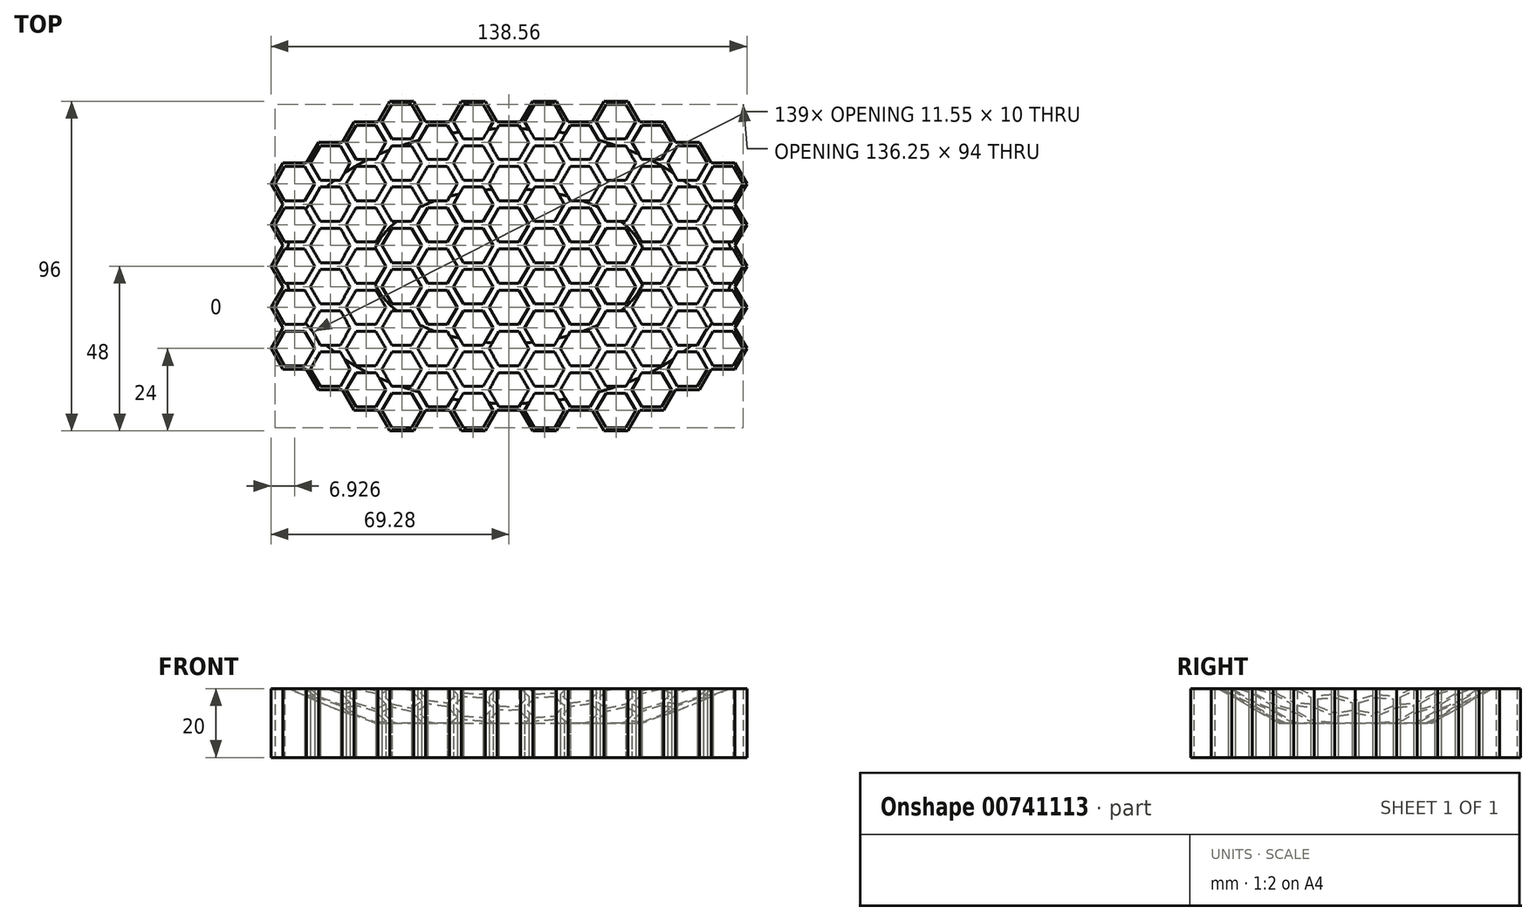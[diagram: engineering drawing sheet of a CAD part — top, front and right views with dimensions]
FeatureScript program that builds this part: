
annotation { "Feature Type Name" : "Feature", "Feature Type Description" : "" }
export const myFeature = defineFeature(function(context is Context, id is Id, definition is map)
    precondition{}
    {
        {
            var Q0;
            Q0=qCreatedBy(makeId("Top.planeOp"),FACE);
            var sketch = newSketch(context, id + "F0", { "sketchPlane" : qUnion([Q0])});
            skLineSegment(sketch, "E0", {"start": v(-3.46, -6) * mm, "end": v(-6.93, 0) * mm, "construction": true});
            skLineSegment(sketch, "E1", {"start": v(-6.93, 0) * mm, "end": v(-3.46, 6) * mm, "construction": true});
            skLineSegment(sketch, "E2", {"start": v(-2.89, 5) * mm, "end": v(2.89, 5) * mm});
            skLineSegment(sketch, "E3", {"start": v(2.89, 5) * mm, "end": v(5.77, 0) * mm});
            skLineSegment(sketch, "E4", {"start": v(5.77, 0) * mm, "end": v(2.89, -5) * mm});
            skLineSegment(sketch, "E5", {"start": v(2.89, -5) * mm, "end": v(-2.89, -5) * mm});
            skLineSegment(sketch, "E6", {"start": v(-2.89, -5) * mm, "end": v(-5.77, 0) * mm});
            skLineSegment(sketch, "E7", {"start": v(-5.77, 0) * mm, "end": v(-2.89, 5) * mm});
            skLineSegment(sketch, "E8", {"start": v(3.46, 6) * mm, "end": v(-3.46, 6) * mm, "construction": true});
            skLineSegment(sketch, "E9", {"start": v(-3.46, -6) * mm, "end": v(3.46, -6) * mm, "construction": true});
            skLineSegment(sketch, "E10", {"start": v(-3.46, 6) * mm, "end": v(-6.93, 12) * mm, "construction": true});
            skLineSegment(sketch, "E11", {"start": v(-6.93, 12) * mm, "end": v(-3.46, 18) * mm, "construction": true});
            skLineSegment(sketch, "E12", {"start": v(-2.89, 17) * mm, "end": v(2.89, 17) * mm});
            skLineSegment(sketch, "E13", {"start": v(2.89, 17) * mm, "end": v(5.77, 12) * mm});
            skLineSegment(sketch, "E14", {"start": v(5.77, 12) * mm, "end": v(2.89, 7) * mm});
            skLineSegment(sketch, "E15", {"start": v(2.89, 7) * mm, "end": v(-2.89, 7) * mm});
            skLineSegment(sketch, "E16", {"start": v(-2.89, 7) * mm, "end": v(-5.77, 12) * mm});
            skLineSegment(sketch, "E17", {"start": v(-5.77, 12) * mm, "end": v(-2.89, 17) * mm});
            skLineSegment(sketch, "E18", {"start": v(3.46, 18) * mm, "end": v(-3.46, 18) * mm, "construction": true});
            skLineSegment(sketch, "E19", {"start": v(3.46, 6) * mm, "end": v(6.93, 12) * mm, "construction": true});
            skLineSegment(sketch, "E20", {"start": v(3.46, 30) * mm, "end": v(6.93, 24) * mm, "construction": true});
            skLineSegment(sketch, "E21", {"start": v(-3.46, 18) * mm, "end": v(-6.93, 24) * mm, "construction": true});
            skLineSegment(sketch, "E22", {"start": v(-6.93, 24) * mm, "end": v(-3.46, 30) * mm, "construction": true});
            skLineSegment(sketch, "E23", {"start": v(-2.89, 29) * mm, "end": v(2.89, 29) * mm});
            skLineSegment(sketch, "E24", {"start": v(2.89, 29) * mm, "end": v(5.77, 24) * mm});
            skLineSegment(sketch, "E25", {"start": v(5.77, 24) * mm, "end": v(2.89, 19) * mm});
            skLineSegment(sketch, "E26", {"start": v(2.89, 19) * mm, "end": v(-2.89, 19) * mm});
            skLineSegment(sketch, "E27", {"start": v(-2.89, 19) * mm, "end": v(-5.77, 24) * mm});
            skLineSegment(sketch, "E28", {"start": v(-5.77, 24) * mm, "end": v(-2.89, 29) * mm});
            skLineSegment(sketch, "E29", {"start": v(3.46, 30) * mm, "end": v(-3.46, 30) * mm, "construction": true});
            skLineSegment(sketch, "E30", {"start": v(-3.46, 30) * mm, "end": v(-6.93, 36) * mm, "construction": true});
            skLineSegment(sketch, "E31", {"start": v(-6.93, 36) * mm, "end": v(-3.46, 42) * mm, "construction": true});
            skLineSegment(sketch, "E32", {"start": v(-2.89, 41) * mm, "end": v(2.89, 41) * mm});
            skLineSegment(sketch, "E33", {"start": v(2.89, 41) * mm, "end": v(5.77, 36) * mm});
            skLineSegment(sketch, "E34", {"start": v(5.77, 36) * mm, "end": v(2.89, 31) * mm});
            skLineSegment(sketch, "E35", {"start": v(2.89, 31) * mm, "end": v(-2.89, 31) * mm});
            skLineSegment(sketch, "E36", {"start": v(-2.89, 31) * mm, "end": v(-5.77, 36) * mm});
            skLineSegment(sketch, "E37", {"start": v(-5.77, 36) * mm, "end": v(-2.89, 41) * mm});
            skLineSegment(sketch, "E38", {"start": v(3.46, 42) * mm, "end": v(-3.46, 42) * mm});
            skLineSegment(sketch, "E39", {"start": v(3.46, 30) * mm, "end": v(6.93, 36) * mm, "construction": true});
            skLineSegment(sketch, "E40", {"start": v(-6.93, -48) * mm, "end": v(-3.46, -42) * mm});
            skLineSegment(sketch, "E41", {"start": v(3.46, -42) * mm, "end": v(-3.46, -42) * mm});
            skLineSegment(sketch, "E42", {"start": v(-3.46, -42) * mm, "end": v(-6.93, -36) * mm, "construction": true});
            skLineSegment(sketch, "E43", {"start": v(-6.93, -36) * mm, "end": v(-3.46, -30) * mm, "construction": true});
            skLineSegment(sketch, "E44", {"start": v(-2.89, -31) * mm, "end": v(2.89, -31) * mm});
            skLineSegment(sketch, "E45", {"start": v(2.89, -31) * mm, "end": v(5.77, -36) * mm});
            skLineSegment(sketch, "E46", {"start": v(5.77, -36) * mm, "end": v(2.89, -41) * mm});
            skLineSegment(sketch, "E47", {"start": v(2.89, -41) * mm, "end": v(-2.89, -41) * mm});
            skLineSegment(sketch, "E48", {"start": v(-2.89, -41) * mm, "end": v(-5.77, -36) * mm});
            skLineSegment(sketch, "E49", {"start": v(-5.77, -36) * mm, "end": v(-2.89, -31) * mm});
            skLineSegment(sketch, "E50", {"start": v(3.46, -30) * mm, "end": v(-3.46, -30) * mm, "construction": true});
            skLineSegment(sketch, "E51", {"start": v(3.46, -42) * mm, "end": v(6.93, -36) * mm, "construction": true});
            skLineSegment(sketch, "E52", {"start": v(3.46, -18) * mm, "end": v(6.93, -24) * mm, "construction": true});
            skLineSegment(sketch, "E53", {"start": v(-3.46, -30) * mm, "end": v(-6.93, -24) * mm, "construction": true});
            skLineSegment(sketch, "E54", {"start": v(-6.93, -24) * mm, "end": v(-3.46, -18) * mm, "construction": true});
            skLineSegment(sketch, "E55", {"start": v(-2.89, -19) * mm, "end": v(2.89, -19) * mm});
            skLineSegment(sketch, "E56", {"start": v(2.89, -19) * mm, "end": v(5.77, -24) * mm});
            skLineSegment(sketch, "E57", {"start": v(5.77, -24) * mm, "end": v(2.89, -29) * mm});
            skLineSegment(sketch, "E58", {"start": v(2.89, -29) * mm, "end": v(-2.89, -29) * mm});
            skLineSegment(sketch, "E59", {"start": v(-2.89, -29) * mm, "end": v(-5.77, -24) * mm});
            skLineSegment(sketch, "E60", {"start": v(-5.77, -24) * mm, "end": v(-2.89, -19) * mm});
            skLineSegment(sketch, "E61", {"start": v(3.46, -18) * mm, "end": v(-3.46, -18) * mm, "construction": true});
            skLineSegment(sketch, "E62", {"start": v(-3.46, -18) * mm, "end": v(-6.93, -12) * mm, "construction": true});
            skLineSegment(sketch, "E63", {"start": v(-6.93, -12) * mm, "end": v(-3.46, -6) * mm, "construction": true});
            skLineSegment(sketch, "E64", {"start": v(-2.89, -7) * mm, "end": v(2.89, -7) * mm});
            skLineSegment(sketch, "E65", {"start": v(2.89, -7) * mm, "end": v(5.77, -12) * mm});
            skLineSegment(sketch, "E66", {"start": v(5.77, -12) * mm, "end": v(2.89, -17) * mm});
            skLineSegment(sketch, "E67", {"start": v(2.89, -17) * mm, "end": v(-2.89, -17) * mm});
            skLineSegment(sketch, "E68", {"start": v(-2.89, -17) * mm, "end": v(-5.77, -12) * mm});
            skLineSegment(sketch, "E69", {"start": v(-5.77, -12) * mm, "end": v(-2.89, -7) * mm});
            skLineSegment(sketch, "E70", {"start": v(3.46, -18) * mm, "end": v(6.93, -12) * mm, "construction": true});
            skLineSegment(sketch, "E71", {"start": v(6.93, 0) * mm, "end": v(3.46, 6) * mm, "construction": true});
            skLineSegment(sketch, "E72", {"start": v(7.5, 11) * mm, "end": v(13.28, 11) * mm});
            skLineSegment(sketch, "E73", {"start": v(13.28, 11) * mm, "end": v(16.17, 6) * mm});
            skLineSegment(sketch, "E74", {"start": v(16.17, 6) * mm, "end": v(13.28, 1) * mm});
            skLineSegment(sketch, "E75", {"start": v(13.28, 1) * mm, "end": v(7.5, 1) * mm});
            skLineSegment(sketch, "E76", {"start": v(7.5, 1) * mm, "end": v(4.62, 6) * mm});
            skLineSegment(sketch, "E77", {"start": v(4.62, 6) * mm, "end": v(7.5, 11) * mm});
            skLineSegment(sketch, "E78", {"start": v(13.86, 12) * mm, "end": v(6.93, 12) * mm, "construction": true});
            skLineSegment(sketch, "E79", {"start": v(6.93, 0) * mm, "end": v(13.86, 0) * mm, "construction": true});
            skLineSegment(sketch, "E80", {"start": v(6.93, 12) * mm, "end": v(3.46, 18) * mm, "construction": true});
            skLineSegment(sketch, "E81", {"start": v(3.46, 18) * mm, "end": v(6.93, 24) * mm, "construction": true});
            skLineSegment(sketch, "E82", {"start": v(7.5, 23) * mm, "end": v(13.28, 23) * mm});
            skLineSegment(sketch, "E83", {"start": v(13.28, 23) * mm, "end": v(16.17, 18) * mm});
            skLineSegment(sketch, "E84", {"start": v(16.17, 18) * mm, "end": v(13.28, 13) * mm});
            skLineSegment(sketch, "E85", {"start": v(13.28, 13) * mm, "end": v(7.5, 13) * mm});
            skLineSegment(sketch, "E86", {"start": v(7.5, 13) * mm, "end": v(4.62, 18) * mm});
            skLineSegment(sketch, "E87", {"start": v(4.62, 18) * mm, "end": v(7.5, 23) * mm});
            skLineSegment(sketch, "E88", {"start": v(13.86, 24) * mm, "end": v(6.93, 24) * mm, "construction": true});
            skLineSegment(sketch, "E89", {"start": v(7.5, 35) * mm, "end": v(13.28, 35) * mm});
            skLineSegment(sketch, "E90", {"start": v(13.28, 35) * mm, "end": v(16.17, 30) * mm});
            skLineSegment(sketch, "E91", {"start": v(16.17, 30) * mm, "end": v(13.28, 25) * mm});
            skLineSegment(sketch, "E92", {"start": v(13.28, 25) * mm, "end": v(7.5, 25) * mm});
            skLineSegment(sketch, "E93", {"start": v(7.5, 25) * mm, "end": v(4.62, 30) * mm});
            skLineSegment(sketch, "E94", {"start": v(4.62, 30) * mm, "end": v(7.5, 35) * mm});
            skLineSegment(sketch, "E95", {"start": v(13.86, 36) * mm, "end": v(6.93, 36) * mm, "construction": true});
            skLineSegment(sketch, "E96", {"start": v(13.86, 24) * mm, "end": v(17.32, 30) * mm, "construction": true});
            skLineSegment(sketch, "E97", {"start": v(13.86, 48) * mm, "end": v(17.32, 42) * mm});
            skLineSegment(sketch, "E98", {"start": v(6.93, 36) * mm, "end": v(3.46, 42) * mm, "construction": true});
            skLineSegment(sketch, "E99", {"start": v(3.46, 42) * mm, "end": v(6.93, 48) * mm});
            skLineSegment(sketch, "E100", {"start": v(7.5, 47) * mm, "end": v(13.28, 47) * mm});
            skLineSegment(sketch, "E101", {"start": v(13.28, 47) * mm, "end": v(16.17, 42) * mm});
            skLineSegment(sketch, "E102", {"start": v(16.17, 42) * mm, "end": v(13.28, 37) * mm});
            skLineSegment(sketch, "E103", {"start": v(13.28, 37) * mm, "end": v(7.5, 37) * mm});
            skLineSegment(sketch, "E104", {"start": v(7.5, 37) * mm, "end": v(4.62, 42) * mm});
            skLineSegment(sketch, "E105", {"start": v(4.62, 42) * mm, "end": v(7.5, 47) * mm});
            skLineSegment(sketch, "E106", {"start": v(13.86, 48) * mm, "end": v(6.93, 48) * mm});
            skLineSegment(sketch, "E107", {"start": v(6.93, -48) * mm, "end": v(3.46, -42) * mm});
            skLineSegment(sketch, "E108", {"start": v(7.5, -37) * mm, "end": v(13.28, -37) * mm});
            skLineSegment(sketch, "E109", {"start": v(13.28, -37) * mm, "end": v(16.17, -42) * mm});
            skLineSegment(sketch, "E110", {"start": v(16.17, -42) * mm, "end": v(13.28, -47) * mm});
            skLineSegment(sketch, "E111", {"start": v(13.28, -47) * mm, "end": v(7.5, -47) * mm});
            skLineSegment(sketch, "E112", {"start": v(7.5, -47) * mm, "end": v(4.62, -42) * mm});
            skLineSegment(sketch, "E113", {"start": v(4.62, -42) * mm, "end": v(7.5, -37) * mm});
            skLineSegment(sketch, "E114", {"start": v(13.86, -36) * mm, "end": v(6.93, -36) * mm, "construction": true});
            skLineSegment(sketch, "E115", {"start": v(6.93, -48) * mm, "end": v(13.86, -48) * mm});
            skLineSegment(sketch, "E116", {"start": v(13.86, -48) * mm, "end": v(17.32, -42) * mm});
            skLineSegment(sketch, "E117", {"start": v(6.93, -36) * mm, "end": v(3.46, -30) * mm, "construction": true});
            skLineSegment(sketch, "E118", {"start": v(3.46, -30) * mm, "end": v(6.93, -24) * mm, "construction": true});
            skLineSegment(sketch, "E119", {"start": v(7.5, -25) * mm, "end": v(13.28, -25) * mm});
            skLineSegment(sketch, "E120", {"start": v(13.28, -25) * mm, "end": v(16.17, -30) * mm});
            skLineSegment(sketch, "E121", {"start": v(16.17, -30) * mm, "end": v(13.28, -35) * mm});
            skLineSegment(sketch, "E122", {"start": v(13.28, -35) * mm, "end": v(7.5, -35) * mm});
            skLineSegment(sketch, "E123", {"start": v(7.5, -35) * mm, "end": v(4.62, -30) * mm});
            skLineSegment(sketch, "E124", {"start": v(4.62, -30) * mm, "end": v(7.5, -25) * mm});
            skLineSegment(sketch, "E125", {"start": v(13.86, -24) * mm, "end": v(6.93, -24) * mm, "construction": true});
            skLineSegment(sketch, "E126", {"start": v(13.86, -36) * mm, "end": v(17.32, -30) * mm, "construction": true});
            skLineSegment(sketch, "E127", {"start": v(13.86, -12) * mm, "end": v(17.32, -18) * mm, "construction": true});
            skLineSegment(sketch, "E128", {"start": v(7.5, -13) * mm, "end": v(13.28, -13) * mm});
            skLineSegment(sketch, "E129", {"start": v(13.28, -13) * mm, "end": v(16.17, -18) * mm});
            skLineSegment(sketch, "E130", {"start": v(16.17, -18) * mm, "end": v(13.28, -23) * mm});
            skLineSegment(sketch, "E131", {"start": v(13.28, -23) * mm, "end": v(7.5, -23) * mm});
            skLineSegment(sketch, "E132", {"start": v(7.5, -23) * mm, "end": v(4.62, -18) * mm});
            skLineSegment(sketch, "E133", {"start": v(4.62, -18) * mm, "end": v(7.5, -13) * mm});
            skLineSegment(sketch, "E134", {"start": v(13.86, -12) * mm, "end": v(6.93, -12) * mm, "construction": true});
            skLineSegment(sketch, "E135", {"start": v(6.93, -12) * mm, "end": v(3.46, -6) * mm, "construction": true});
            skLineSegment(sketch, "E136", {"start": v(3.46, -6) * mm, "end": v(6.93, 0) * mm, "construction": true});
            skLineSegment(sketch, "E137", {"start": v(7.5, -1) * mm, "end": v(13.28, -1) * mm});
            skLineSegment(sketch, "E138", {"start": v(13.28, -1) * mm, "end": v(16.17, -6) * mm});
            skLineSegment(sketch, "E139", {"start": v(16.17, -6) * mm, "end": v(13.28, -11) * mm});
            skLineSegment(sketch, "E140", {"start": v(13.28, -11) * mm, "end": v(7.5, -11) * mm});
            skLineSegment(sketch, "E141", {"start": v(7.5, -11) * mm, "end": v(4.62, -6) * mm});
            skLineSegment(sketch, "E142", {"start": v(4.62, -6) * mm, "end": v(7.5, -1) * mm});
            skLineSegment(sketch, "E143", {"start": v(13.86, -12) * mm, "end": v(17.32, -6) * mm, "construction": true});
            skLineSegment(sketch, "E144", {"start": v(17.32, -6) * mm, "end": v(13.86, 0) * mm, "construction": true});
            skLineSegment(sketch, "E145", {"start": v(13.86, 0) * mm, "end": v(17.32, 6) * mm, "construction": true});
            skLineSegment(sketch, "E146", {"start": v(17.9, 5) * mm, "end": v(23.67, 5) * mm});
            skLineSegment(sketch, "E147", {"start": v(23.67, 5) * mm, "end": v(26.56, 0) * mm});
            skLineSegment(sketch, "E148", {"start": v(26.56, 0) * mm, "end": v(23.67, -5) * mm});
            skLineSegment(sketch, "E149", {"start": v(23.67, -5) * mm, "end": v(17.9, -5) * mm});
            skLineSegment(sketch, "E150", {"start": v(17.9, -5) * mm, "end": v(15.01, 0) * mm});
            skLineSegment(sketch, "E151", {"start": v(15.01, 0) * mm, "end": v(17.9, 5) * mm});
            skLineSegment(sketch, "E152", {"start": v(24.25, 6) * mm, "end": v(17.32, 6) * mm, "construction": true});
            skLineSegment(sketch, "E153", {"start": v(17.32, -6) * mm, "end": v(24.25, -6) * mm, "construction": true});
            skLineSegment(sketch, "E154", {"start": v(17.32, 6) * mm, "end": v(13.86, 12) * mm, "construction": true});
            skLineSegment(sketch, "E155", {"start": v(13.86, 12) * mm, "end": v(17.32, 18) * mm, "construction": true});
            skLineSegment(sketch, "E156", {"start": v(17.9, 17) * mm, "end": v(23.67, 17) * mm});
            skLineSegment(sketch, "E157", {"start": v(23.67, 17) * mm, "end": v(26.56, 12) * mm});
            skLineSegment(sketch, "E158", {"start": v(26.56, 12) * mm, "end": v(23.67, 7) * mm});
            skLineSegment(sketch, "E159", {"start": v(23.67, 7) * mm, "end": v(17.9, 7) * mm});
            skLineSegment(sketch, "E160", {"start": v(17.9, 7) * mm, "end": v(15.01, 12) * mm});
            skLineSegment(sketch, "E161", {"start": v(15.01, 12) * mm, "end": v(17.9, 17) * mm});
            skLineSegment(sketch, "E162", {"start": v(24.25, 18) * mm, "end": v(17.32, 18) * mm, "construction": true});
            skLineSegment(sketch, "E163", {"start": v(24.25, 6) * mm, "end": v(27.71, 12) * mm, "construction": true});
            skLineSegment(sketch, "E164", {"start": v(24.25, 30) * mm, "end": v(27.71, 24) * mm, "construction": true});
            skLineSegment(sketch, "E165", {"start": v(17.32, 18) * mm, "end": v(13.86, 24) * mm, "construction": true});
            skLineSegment(sketch, "E166", {"start": v(17.9, 29) * mm, "end": v(23.67, 29) * mm});
            skLineSegment(sketch, "E167", {"start": v(23.67, 29) * mm, "end": v(26.56, 24) * mm});
            skLineSegment(sketch, "E168", {"start": v(26.56, 24) * mm, "end": v(23.67, 19) * mm});
            skLineSegment(sketch, "E169", {"start": v(23.67, 19) * mm, "end": v(17.9, 19) * mm});
            skLineSegment(sketch, "E170", {"start": v(17.9, 19) * mm, "end": v(15.01, 24) * mm});
            skLineSegment(sketch, "E171", {"start": v(15.01, 24) * mm, "end": v(17.9, 29) * mm});
            skLineSegment(sketch, "E172", {"start": v(24.25, 30) * mm, "end": v(17.32, 30) * mm, "construction": true});
            skLineSegment(sketch, "E173", {"start": v(17.32, 30) * mm, "end": v(13.86, 36) * mm, "construction": true});
            skLineSegment(sketch, "E174", {"start": v(13.86, 36) * mm, "end": v(17.32, 42) * mm, "construction": true});
            skLineSegment(sketch, "E175", {"start": v(17.9, 41) * mm, "end": v(23.67, 41) * mm});
            skLineSegment(sketch, "E176", {"start": v(23.67, 41) * mm, "end": v(26.56, 36) * mm});
            skLineSegment(sketch, "E177", {"start": v(26.56, 36) * mm, "end": v(23.67, 31) * mm});
            skLineSegment(sketch, "E178", {"start": v(23.67, 31) * mm, "end": v(17.9, 31) * mm});
            skLineSegment(sketch, "E179", {"start": v(17.9, 31) * mm, "end": v(15.01, 36) * mm});
            skLineSegment(sketch, "E180", {"start": v(15.01, 36) * mm, "end": v(17.9, 41) * mm});
            skLineSegment(sketch, "E181", {"start": v(24.25, 42) * mm, "end": v(17.32, 42) * mm});
            skLineSegment(sketch, "E182", {"start": v(24.25, 30) * mm, "end": v(27.71, 36) * mm, "construction": true});
            skLineSegment(sketch, "E183", {"start": v(24.25, -42) * mm, "end": v(17.32, -42) * mm});
            skLineSegment(sketch, "E184", {"start": v(17.32, -42) * mm, "end": v(13.86, -36) * mm, "construction": true});
            skLineSegment(sketch, "E185", {"start": v(17.9, -31) * mm, "end": v(23.67, -31) * mm});
            skLineSegment(sketch, "E186", {"start": v(23.67, -31) * mm, "end": v(26.56, -36) * mm});
            skLineSegment(sketch, "E187", {"start": v(26.56, -36) * mm, "end": v(23.67, -41) * mm});
            skLineSegment(sketch, "E188", {"start": v(23.67, -41) * mm, "end": v(17.9, -41) * mm});
            skLineSegment(sketch, "E189", {"start": v(17.9, -41) * mm, "end": v(15.01, -36) * mm});
            skLineSegment(sketch, "E190", {"start": v(15.01, -36) * mm, "end": v(17.9, -31) * mm});
            skLineSegment(sketch, "E191", {"start": v(24.25, -30) * mm, "end": v(17.32, -30) * mm, "construction": true});
            skLineSegment(sketch, "E192", {"start": v(24.25, -42) * mm, "end": v(27.71, -36) * mm, "construction": true});
            skLineSegment(sketch, "E193", {"start": v(24.25, -18) * mm, "end": v(27.71, -24) * mm, "construction": true});
            skLineSegment(sketch, "E194", {"start": v(17.32, -30) * mm, "end": v(13.86, -24) * mm, "construction": true});
            skLineSegment(sketch, "E195", {"start": v(13.86, -24) * mm, "end": v(17.32, -18) * mm, "construction": true});
            skLineSegment(sketch, "E196", {"start": v(17.9, -19) * mm, "end": v(23.67, -19) * mm});
            skLineSegment(sketch, "E197", {"start": v(23.67, -19) * mm, "end": v(26.56, -24) * mm});
            skLineSegment(sketch, "E198", {"start": v(26.56, -24) * mm, "end": v(23.67, -29) * mm});
            skLineSegment(sketch, "E199", {"start": v(23.67, -29) * mm, "end": v(17.9, -29) * mm});
            skLineSegment(sketch, "E200", {"start": v(17.9, -29) * mm, "end": v(15.01, -24) * mm});
            skLineSegment(sketch, "E201", {"start": v(15.01, -24) * mm, "end": v(17.9, -19) * mm});
            skLineSegment(sketch, "E202", {"start": v(24.25, -18) * mm, "end": v(17.32, -18) * mm, "construction": true});
            skLineSegment(sketch, "E203", {"start": v(17.9, -7) * mm, "end": v(23.67, -7) * mm});
            skLineSegment(sketch, "E204", {"start": v(23.67, -7) * mm, "end": v(26.56, -12) * mm});
            skLineSegment(sketch, "E205", {"start": v(26.56, -12) * mm, "end": v(23.67, -17) * mm});
            skLineSegment(sketch, "E206", {"start": v(23.67, -17) * mm, "end": v(17.9, -17) * mm});
            skLineSegment(sketch, "E207", {"start": v(17.9, -17) * mm, "end": v(15.01, -12) * mm});
            skLineSegment(sketch, "E208", {"start": v(15.01, -12) * mm, "end": v(17.9, -7) * mm});
            skLineSegment(sketch, "E209", {"start": v(24.25, -18) * mm, "end": v(27.71, -12) * mm, "construction": true});
            skLineSegment(sketch, "E210", {"start": v(34.64, 12) * mm, "end": v(38.1, 6) * mm, "construction": true});
            skLineSegment(sketch, "E211", {"start": v(27.71, 0) * mm, "end": v(24.25, 6) * mm, "construction": true});
            skLineSegment(sketch, "E212", {"start": v(28.3, 11) * mm, "end": v(34.06, 11) * mm});
            skLineSegment(sketch, "E213", {"start": v(34.06, 11) * mm, "end": v(36.95, 6) * mm});
            skLineSegment(sketch, "E214", {"start": v(36.95, 6) * mm, "end": v(34.06, 1) * mm});
            skLineSegment(sketch, "E215", {"start": v(34.06, 1) * mm, "end": v(28.3, 1) * mm});
            skLineSegment(sketch, "E216", {"start": v(28.3, 1) * mm, "end": v(25.4, 6) * mm});
            skLineSegment(sketch, "E217", {"start": v(25.4, 6) * mm, "end": v(28.3, 11) * mm});
            skLineSegment(sketch, "E218", {"start": v(34.64, 12) * mm, "end": v(27.71, 12) * mm, "construction": true});
            skLineSegment(sketch, "E219", {"start": v(27.71, 0) * mm, "end": v(34.64, 0) * mm, "construction": true});
            skLineSegment(sketch, "E220", {"start": v(34.64, 0) * mm, "end": v(38.1, 6) * mm, "construction": true});
            skLineSegment(sketch, "E221", {"start": v(34.64, 24) * mm, "end": v(38.1, 18) * mm, "construction": true});
            skLineSegment(sketch, "E222", {"start": v(27.71, 12) * mm, "end": v(24.25, 18) * mm, "construction": true});
            skLineSegment(sketch, "E223", {"start": v(24.25, 18) * mm, "end": v(27.71, 24) * mm, "construction": true});
            skLineSegment(sketch, "E224", {"start": v(28.3, 23) * mm, "end": v(34.06, 23) * mm});
            skLineSegment(sketch, "E225", {"start": v(34.06, 23) * mm, "end": v(36.95, 18) * mm});
            skLineSegment(sketch, "E226", {"start": v(36.95, 18) * mm, "end": v(34.06, 13) * mm});
            skLineSegment(sketch, "E227", {"start": v(34.06, 13) * mm, "end": v(28.3, 13) * mm});
            skLineSegment(sketch, "E228", {"start": v(28.3, 13) * mm, "end": v(25.4, 18) * mm});
            skLineSegment(sketch, "E229", {"start": v(25.4, 18) * mm, "end": v(28.3, 23) * mm});
            skLineSegment(sketch, "E230", {"start": v(34.64, 24) * mm, "end": v(27.71, 24) * mm, "construction": true});
            skLineSegment(sketch, "E231", {"start": v(34.64, 12) * mm, "end": v(38.1, 18) * mm, "construction": true});
            skLineSegment(sketch, "E232", {"start": v(34.64, 36) * mm, "end": v(38.1, 30) * mm, "construction": true});
            skLineSegment(sketch, "E233", {"start": v(28.3, 35) * mm, "end": v(34.06, 35) * mm});
            skLineSegment(sketch, "E234", {"start": v(34.06, 35) * mm, "end": v(36.95, 30) * mm});
            skLineSegment(sketch, "E235", {"start": v(36.95, 30) * mm, "end": v(34.06, 25) * mm});
            skLineSegment(sketch, "E236", {"start": v(34.06, 25) * mm, "end": v(28.3, 25) * mm});
            skLineSegment(sketch, "E237", {"start": v(28.3, 25) * mm, "end": v(25.4, 30) * mm});
            skLineSegment(sketch, "E238", {"start": v(25.4, 30) * mm, "end": v(28.3, 35) * mm});
            skLineSegment(sketch, "E239", {"start": v(34.64, 36) * mm, "end": v(27.71, 36) * mm, "construction": true});
            skLineSegment(sketch, "E240", {"start": v(34.64, 24) * mm, "end": v(38.1, 30) * mm, "construction": true});
            skLineSegment(sketch, "E241", {"start": v(34.64, 48) * mm, "end": v(38.1, 42) * mm});
            skLineSegment(sketch, "E242", {"start": v(27.71, 36) * mm, "end": v(24.25, 42) * mm, "construction": true});
            skLineSegment(sketch, "E243", {"start": v(24.25, 42) * mm, "end": v(27.71, 48) * mm});
            skLineSegment(sketch, "E244", {"start": v(28.3, 47) * mm, "end": v(34.06, 47) * mm});
            skLineSegment(sketch, "E245", {"start": v(34.06, 47) * mm, "end": v(36.95, 42) * mm});
            skLineSegment(sketch, "E246", {"start": v(36.95, 42) * mm, "end": v(34.06, 37) * mm});
            skLineSegment(sketch, "E247", {"start": v(34.06, 37) * mm, "end": v(28.3, 37) * mm});
            skLineSegment(sketch, "E248", {"start": v(28.3, 37) * mm, "end": v(25.4, 42) * mm});
            skLineSegment(sketch, "E249", {"start": v(25.4, 42) * mm, "end": v(28.3, 47) * mm});
            skLineSegment(sketch, "E250", {"start": v(34.64, 48) * mm, "end": v(27.71, 48) * mm});
            skLineSegment(sketch, "E251", {"start": v(34.64, 36) * mm, "end": v(38.1, 42) * mm, "construction": true});
            skLineSegment(sketch, "E252", {"start": v(34.64, -36) * mm, "end": v(38.1, -42) * mm, "construction": true});
            skLineSegment(sketch, "E253", {"start": v(27.71, -48) * mm, "end": v(24.25, -42) * mm});
            skLineSegment(sketch, "E254", {"start": v(28.3, -37) * mm, "end": v(34.06, -37) * mm});
            skLineSegment(sketch, "E255", {"start": v(34.06, -37) * mm, "end": v(36.95, -42) * mm});
            skLineSegment(sketch, "E256", {"start": v(36.95, -42) * mm, "end": v(34.06, -47) * mm});
            skLineSegment(sketch, "E257", {"start": v(34.06, -47) * mm, "end": v(28.3, -47) * mm});
            skLineSegment(sketch, "E258", {"start": v(28.3, -47) * mm, "end": v(25.4, -42) * mm});
            skLineSegment(sketch, "E259", {"start": v(25.4, -42) * mm, "end": v(28.3, -37) * mm});
            skLineSegment(sketch, "E260", {"start": v(34.64, -36) * mm, "end": v(27.71, -36) * mm, "construction": true});
            skLineSegment(sketch, "E261", {"start": v(27.71, -48) * mm, "end": v(34.64, -48) * mm});
            skLineSegment(sketch, "E262", {"start": v(34.64, -48) * mm, "end": v(38.1, -42) * mm});
            skLineSegment(sketch, "E263", {"start": v(34.64, -24) * mm, "end": v(38.1, -30) * mm, "construction": true});
            skLineSegment(sketch, "E264", {"start": v(27.71, -36) * mm, "end": v(24.25, -30) * mm, "construction": true});
            skLineSegment(sketch, "E265", {"start": v(24.25, -30) * mm, "end": v(27.71, -24) * mm, "construction": true});
            skLineSegment(sketch, "E266", {"start": v(28.3, -25) * mm, "end": v(34.06, -25) * mm});
            skLineSegment(sketch, "E267", {"start": v(34.06, -25) * mm, "end": v(36.95, -30) * mm});
            skLineSegment(sketch, "E268", {"start": v(36.95, -30) * mm, "end": v(34.06, -35) * mm});
            skLineSegment(sketch, "E269", {"start": v(34.06, -35) * mm, "end": v(28.3, -35) * mm});
            skLineSegment(sketch, "E270", {"start": v(28.3, -35) * mm, "end": v(25.4, -30) * mm});
            skLineSegment(sketch, "E271", {"start": v(25.4, -30) * mm, "end": v(28.3, -25) * mm});
            skLineSegment(sketch, "E272", {"start": v(34.64, -24) * mm, "end": v(27.71, -24) * mm, "construction": true});
            skLineSegment(sketch, "E273", {"start": v(34.64, -36) * mm, "end": v(38.1, -30) * mm, "construction": true});
            skLineSegment(sketch, "E274", {"start": v(34.64, -12) * mm, "end": v(38.1, -18) * mm, "construction": true});
            skLineSegment(sketch, "E275", {"start": v(28.3, -13) * mm, "end": v(34.06, -13) * mm});
            skLineSegment(sketch, "E276", {"start": v(34.06, -13) * mm, "end": v(36.95, -18) * mm});
            skLineSegment(sketch, "E277", {"start": v(36.95, -18) * mm, "end": v(34.06, -23) * mm});
            skLineSegment(sketch, "E278", {"start": v(34.06, -23) * mm, "end": v(28.3, -23) * mm});
            skLineSegment(sketch, "E279", {"start": v(28.3, -23) * mm, "end": v(25.4, -18) * mm});
            skLineSegment(sketch, "E280", {"start": v(25.4, -18) * mm, "end": v(28.3, -13) * mm});
            skLineSegment(sketch, "E281", {"start": v(34.64, -12) * mm, "end": v(27.71, -12) * mm, "construction": true});
            skLineSegment(sketch, "E282", {"start": v(34.64, -24) * mm, "end": v(38.1, -18) * mm, "construction": true});
            skLineSegment(sketch, "E283", {"start": v(34.64, 0) * mm, "end": v(38.1, -6) * mm, "construction": true});
            skLineSegment(sketch, "E284", {"start": v(27.71, -12) * mm, "end": v(24.25, -6) * mm, "construction": true});
            skLineSegment(sketch, "E285", {"start": v(24.25, -6) * mm, "end": v(27.71, 0) * mm, "construction": true});
            skLineSegment(sketch, "E286", {"start": v(28.3, -1) * mm, "end": v(34.06, -1) * mm});
            skLineSegment(sketch, "E287", {"start": v(34.06, -1) * mm, "end": v(36.95, -6) * mm});
            skLineSegment(sketch, "E288", {"start": v(36.95, -6) * mm, "end": v(34.06, -11) * mm});
            skLineSegment(sketch, "E289", {"start": v(34.06, -11) * mm, "end": v(28.3, -11) * mm});
            skLineSegment(sketch, "E290", {"start": v(28.3, -11) * mm, "end": v(25.4, -6) * mm});
            skLineSegment(sketch, "E291", {"start": v(25.4, -6) * mm, "end": v(28.3, -1) * mm});
            skLineSegment(sketch, "E292", {"start": v(34.64, -12) * mm, "end": v(38.1, -6) * mm, "construction": true});
            skLineSegment(sketch, "E293", {"start": v(38.1, -6) * mm, "end": v(34.64, 0) * mm, "construction": true});
            skLineSegment(sketch, "E294", {"start": v(38.68, 5) * mm, "end": v(44.46, 5) * mm});
            skLineSegment(sketch, "E295", {"start": v(44.46, 5) * mm, "end": v(47.34, 0) * mm});
            skLineSegment(sketch, "E296", {"start": v(47.34, 0) * mm, "end": v(44.46, -5) * mm});
            skLineSegment(sketch, "E297", {"start": v(44.46, -5) * mm, "end": v(38.68, -5) * mm});
            skLineSegment(sketch, "E298", {"start": v(38.68, -5) * mm, "end": v(35.8, 0) * mm});
            skLineSegment(sketch, "E299", {"start": v(35.8, 0) * mm, "end": v(38.68, 5) * mm});
            skLineSegment(sketch, "E300", {"start": v(45.03, 6) * mm, "end": v(38.1, 6) * mm, "construction": true});
            skLineSegment(sketch, "E301", {"start": v(38.1, -6) * mm, "end": v(45.03, -6) * mm, "construction": true});
            skLineSegment(sketch, "E302", {"start": v(38.1, 6) * mm, "end": v(34.64, 12) * mm, "construction": true});
            skLineSegment(sketch, "E303", {"start": v(38.68, 17) * mm, "end": v(44.46, 17) * mm});
            skLineSegment(sketch, "E304", {"start": v(44.46, 17) * mm, "end": v(47.34, 12) * mm});
            skLineSegment(sketch, "E305", {"start": v(47.34, 12) * mm, "end": v(44.46, 7) * mm});
            skLineSegment(sketch, "E306", {"start": v(44.46, 7) * mm, "end": v(38.68, 7) * mm});
            skLineSegment(sketch, "E307", {"start": v(38.68, 7) * mm, "end": v(35.8, 12) * mm});
            skLineSegment(sketch, "E308", {"start": v(35.8, 12) * mm, "end": v(38.68, 17) * mm});
            skLineSegment(sketch, "E309", {"start": v(45.03, 18) * mm, "end": v(38.1, 18) * mm, "construction": true});
            skLineSegment(sketch, "E310", {"start": v(45.03, 6) * mm, "end": v(48.5, 12) * mm, "construction": true});
            skLineSegment(sketch, "E311", {"start": v(45.03, 30) * mm, "end": v(48.5, 24) * mm, "construction": true});
            skLineSegment(sketch, "E312", {"start": v(38.1, 18) * mm, "end": v(34.64, 24) * mm, "construction": true});
            skLineSegment(sketch, "E313", {"start": v(38.68, 29) * mm, "end": v(44.46, 29) * mm});
            skLineSegment(sketch, "E314", {"start": v(44.46, 29) * mm, "end": v(47.34, 24) * mm});
            skLineSegment(sketch, "E315", {"start": v(47.34, 24) * mm, "end": v(44.46, 19) * mm});
            skLineSegment(sketch, "E316", {"start": v(44.46, 19) * mm, "end": v(38.68, 19) * mm});
            skLineSegment(sketch, "E317", {"start": v(38.68, 19) * mm, "end": v(35.8, 24) * mm});
            skLineSegment(sketch, "E318", {"start": v(35.8, 24) * mm, "end": v(38.68, 29) * mm});
            skLineSegment(sketch, "E319", {"start": v(45.03, 30) * mm, "end": v(38.1, 30) * mm, "construction": true});
            skLineSegment(sketch, "E320", {"start": v(38.1, 30) * mm, "end": v(34.64, 36) * mm, "construction": true});
            skLineSegment(sketch, "E321", {"start": v(38.68, 41) * mm, "end": v(44.46, 41) * mm});
            skLineSegment(sketch, "E322", {"start": v(44.46, 41) * mm, "end": v(47.34, 36) * mm});
            skLineSegment(sketch, "E323", {"start": v(47.34, 36) * mm, "end": v(44.46, 31) * mm});
            skLineSegment(sketch, "E324", {"start": v(44.46, 31) * mm, "end": v(38.68, 31) * mm});
            skLineSegment(sketch, "E325", {"start": v(38.68, 31) * mm, "end": v(35.8, 36) * mm});
            skLineSegment(sketch, "E326", {"start": v(35.8, 36) * mm, "end": v(38.68, 41) * mm});
            skLineSegment(sketch, "E327", {"start": v(45.03, 42) * mm, "end": v(38.1, 42) * mm});
            skLineSegment(sketch, "E328", {"start": v(45.03, 30) * mm, "end": v(48.5, 36) * mm, "construction": true});
            skLineSegment(sketch, "E329", {"start": v(34.64, -48) * mm, "end": v(38.1, -42) * mm, "construction": true});
            skLineSegment(sketch, "E330", {"start": v(45.03, -42) * mm, "end": v(38.1, -42) * mm});
            skLineSegment(sketch, "E331", {"start": v(38.1, -42) * mm, "end": v(34.64, -36) * mm, "construction": true});
            skLineSegment(sketch, "E332", {"start": v(38.68, -31) * mm, "end": v(44.46, -31) * mm});
            skLineSegment(sketch, "E333", {"start": v(44.46, -31) * mm, "end": v(47.34, -36) * mm});
            skLineSegment(sketch, "E334", {"start": v(47.34, -36) * mm, "end": v(44.46, -41) * mm});
            skLineSegment(sketch, "E335", {"start": v(44.46, -41) * mm, "end": v(38.68, -41) * mm});
            skLineSegment(sketch, "E336", {"start": v(38.68, -41) * mm, "end": v(35.8, -36) * mm});
            skLineSegment(sketch, "E337", {"start": v(35.8, -36) * mm, "end": v(38.68, -31) * mm});
            skLineSegment(sketch, "E338", {"start": v(45.03, -30) * mm, "end": v(38.1, -30) * mm, "construction": true});
            skLineSegment(sketch, "E339", {"start": v(45.03, -42) * mm, "end": v(48.5, -36) * mm});
            skLineSegment(sketch, "E340", {"start": v(45.03, -18) * mm, "end": v(48.5, -24) * mm, "construction": true});
            skLineSegment(sketch, "E341", {"start": v(38.1, -30) * mm, "end": v(34.64, -24) * mm, "construction": true});
            skLineSegment(sketch, "E342", {"start": v(38.68, -19) * mm, "end": v(44.46, -19) * mm});
            skLineSegment(sketch, "E343", {"start": v(44.46, -19) * mm, "end": v(47.34, -24) * mm});
            skLineSegment(sketch, "E344", {"start": v(47.34, -24) * mm, "end": v(44.46, -29) * mm});
            skLineSegment(sketch, "E345", {"start": v(44.46, -29) * mm, "end": v(38.68, -29) * mm});
            skLineSegment(sketch, "E346", {"start": v(38.68, -29) * mm, "end": v(35.8, -24) * mm});
            skLineSegment(sketch, "E347", {"start": v(35.8, -24) * mm, "end": v(38.68, -19) * mm});
            skLineSegment(sketch, "E348", {"start": v(45.03, -18) * mm, "end": v(38.1, -18) * mm, "construction": true});
            skLineSegment(sketch, "E349", {"start": v(38.1, -18) * mm, "end": v(34.64, -12) * mm, "construction": true});
            skLineSegment(sketch, "E350", {"start": v(38.68, -7) * mm, "end": v(44.46, -7) * mm});
            skLineSegment(sketch, "E351", {"start": v(44.46, -7) * mm, "end": v(47.34, -12) * mm});
            skLineSegment(sketch, "E352", {"start": v(47.34, -12) * mm, "end": v(44.46, -17) * mm});
            skLineSegment(sketch, "E353", {"start": v(44.46, -17) * mm, "end": v(38.68, -17) * mm});
            skLineSegment(sketch, "E354", {"start": v(38.68, -17) * mm, "end": v(35.8, -12) * mm});
            skLineSegment(sketch, "E355", {"start": v(35.8, -12) * mm, "end": v(38.68, -7) * mm});
            skLineSegment(sketch, "E356", {"start": v(45.03, -18) * mm, "end": v(48.5, -12) * mm, "construction": true});
            skLineSegment(sketch, "E357", {"start": v(48.5, 0) * mm, "end": v(45.03, 6) * mm, "construction": true});
            skLineSegment(sketch, "E358", {"start": v(49.07, 11) * mm, "end": v(54.85, 11) * mm});
            skLineSegment(sketch, "E359", {"start": v(54.85, 11) * mm, "end": v(57.74, 6) * mm});
            skLineSegment(sketch, "E360", {"start": v(57.74, 6) * mm, "end": v(54.85, 1) * mm});
            skLineSegment(sketch, "E361", {"start": v(54.85, 1) * mm, "end": v(49.07, 1) * mm});
            skLineSegment(sketch, "E362", {"start": v(49.07, 1) * mm, "end": v(46.19, 6) * mm});
            skLineSegment(sketch, "E363", {"start": v(46.19, 6) * mm, "end": v(49.07, 11) * mm});
            skLineSegment(sketch, "E364", {"start": v(55.43, 12) * mm, "end": v(48.5, 12) * mm, "construction": true});
            skLineSegment(sketch, "E365", {"start": v(48.5, 0) * mm, "end": v(55.43, 0) * mm, "construction": true});
            skLineSegment(sketch, "E366", {"start": v(48.5, 12) * mm, "end": v(45.03, 18) * mm, "construction": true});
            skLineSegment(sketch, "E367", {"start": v(45.03, 18) * mm, "end": v(48.5, 24) * mm, "construction": true});
            skLineSegment(sketch, "E368", {"start": v(49.07, 23) * mm, "end": v(54.85, 23) * mm});
            skLineSegment(sketch, "E369", {"start": v(54.85, 23) * mm, "end": v(57.74, 18) * mm});
            skLineSegment(sketch, "E370", {"start": v(57.74, 18) * mm, "end": v(54.85, 13) * mm});
            skLineSegment(sketch, "E371", {"start": v(54.85, 13) * mm, "end": v(49.07, 13) * mm});
            skLineSegment(sketch, "E372", {"start": v(49.07, 13) * mm, "end": v(46.19, 18) * mm});
            skLineSegment(sketch, "E373", {"start": v(46.19, 18) * mm, "end": v(49.07, 23) * mm});
            skLineSegment(sketch, "E374", {"start": v(55.43, 24) * mm, "end": v(48.5, 24) * mm, "construction": true});
            skLineSegment(sketch, "E375", {"start": v(49.07, 35) * mm, "end": v(54.85, 35) * mm});
            skLineSegment(sketch, "E376", {"start": v(54.85, 35) * mm, "end": v(57.74, 30) * mm});
            skLineSegment(sketch, "E377", {"start": v(57.74, 30) * mm, "end": v(54.85, 25) * mm});
            skLineSegment(sketch, "E378", {"start": v(54.85, 25) * mm, "end": v(49.07, 25) * mm});
            skLineSegment(sketch, "E379", {"start": v(49.07, 25) * mm, "end": v(46.19, 30) * mm});
            skLineSegment(sketch, "E380", {"start": v(46.19, 30) * mm, "end": v(49.07, 35) * mm});
            skLineSegment(sketch, "E381", {"start": v(55.43, 36) * mm, "end": v(48.5, 36) * mm});
            skLineSegment(sketch, "E382", {"start": v(55.43, 24) * mm, "end": v(58.89, 30) * mm, "construction": true});
            skLineSegment(sketch, "E383", {"start": v(48.5, 36) * mm, "end": v(45.03, 42) * mm});
            skLineSegment(sketch, "E384", {"start": v(55.43, -36) * mm, "end": v(48.5, -36) * mm});
            skLineSegment(sketch, "E385", {"start": v(48.5, -36) * mm, "end": v(45.03, -30) * mm, "construction": true});
            skLineSegment(sketch, "E386", {"start": v(45.03, -30) * mm, "end": v(48.5, -24) * mm, "construction": true});
            skLineSegment(sketch, "E387", {"start": v(49.07, -25) * mm, "end": v(54.85, -25) * mm});
            skLineSegment(sketch, "E388", {"start": v(54.85, -25) * mm, "end": v(57.74, -30) * mm});
            skLineSegment(sketch, "E389", {"start": v(57.74, -30) * mm, "end": v(54.85, -35) * mm});
            skLineSegment(sketch, "E390", {"start": v(54.85, -35) * mm, "end": v(49.07, -35) * mm});
            skLineSegment(sketch, "E391", {"start": v(49.07, -35) * mm, "end": v(46.19, -30) * mm});
            skLineSegment(sketch, "E392", {"start": v(46.19, -30) * mm, "end": v(49.07, -25) * mm});
            skLineSegment(sketch, "E393", {"start": v(55.43, -24) * mm, "end": v(48.5, -24) * mm, "construction": true});
            skLineSegment(sketch, "E394", {"start": v(55.43, -36) * mm, "end": v(58.89, -30) * mm});
            skLineSegment(sketch, "E395", {"start": v(55.43, -12) * mm, "end": v(58.89, -18) * mm, "construction": true});
            skLineSegment(sketch, "E396", {"start": v(49.07, -13) * mm, "end": v(54.85, -13) * mm});
            skLineSegment(sketch, "E397", {"start": v(54.85, -13) * mm, "end": v(57.74, -18) * mm});
            skLineSegment(sketch, "E398", {"start": v(57.74, -18) * mm, "end": v(54.85, -23) * mm});
            skLineSegment(sketch, "E399", {"start": v(54.85, -23) * mm, "end": v(49.07, -23) * mm});
            skLineSegment(sketch, "E400", {"start": v(49.07, -23) * mm, "end": v(46.19, -18) * mm});
            skLineSegment(sketch, "E401", {"start": v(46.19, -18) * mm, "end": v(49.07, -13) * mm});
            skLineSegment(sketch, "E402", {"start": v(55.43, -12) * mm, "end": v(48.5, -12) * mm, "construction": true});
            skLineSegment(sketch, "E403", {"start": v(48.5, -12) * mm, "end": v(45.03, -6) * mm, "construction": true});
            skLineSegment(sketch, "E404", {"start": v(45.03, -6) * mm, "end": v(48.5, 0) * mm, "construction": true});
            skLineSegment(sketch, "E405", {"start": v(49.07, -1) * mm, "end": v(54.85, -1) * mm});
            skLineSegment(sketch, "E406", {"start": v(54.85, -1) * mm, "end": v(57.74, -6) * mm});
            skLineSegment(sketch, "E407", {"start": v(57.74, -6) * mm, "end": v(54.85, -11) * mm});
            skLineSegment(sketch, "E408", {"start": v(54.85, -11) * mm, "end": v(49.07, -11) * mm});
            skLineSegment(sketch, "E409", {"start": v(49.07, -11) * mm, "end": v(46.19, -6) * mm});
            skLineSegment(sketch, "E410", {"start": v(46.19, -6) * mm, "end": v(49.07, -1) * mm});
            skLineSegment(sketch, "E411", {"start": v(55.43, -12) * mm, "end": v(58.89, -6) * mm, "construction": true});
            skLineSegment(sketch, "E412", {"start": v(58.89, -6) * mm, "end": v(55.43, 0) * mm, "construction": true});
            skLineSegment(sketch, "E413", {"start": v(55.43, 0) * mm, "end": v(58.89, 6) * mm, "construction": true});
            skLineSegment(sketch, "E414", {"start": v(59.47, 5) * mm, "end": v(65.24, 5) * mm});
            skLineSegment(sketch, "E415", {"start": v(65.24, 5) * mm, "end": v(68.13, 0) * mm});
            skLineSegment(sketch, "E416", {"start": v(68.13, 0) * mm, "end": v(65.24, -5) * mm});
            skLineSegment(sketch, "E417", {"start": v(65.24, -5) * mm, "end": v(59.47, -5) * mm});
            skLineSegment(sketch, "E418", {"start": v(59.47, -5) * mm, "end": v(56.58, 0) * mm});
            skLineSegment(sketch, "E419", {"start": v(56.58, 0) * mm, "end": v(59.47, 5) * mm});
            skLineSegment(sketch, "E420", {"start": v(65.82, 6) * mm, "end": v(58.89, 6) * mm, "construction": true});
            skLineSegment(sketch, "E421", {"start": v(58.89, -6) * mm, "end": v(65.82, -6) * mm, "construction": true});
            skLineSegment(sketch, "E422", {"start": v(58.89, 6) * mm, "end": v(55.43, 12) * mm, "construction": true});
            skLineSegment(sketch, "E423", {"start": v(55.43, 12) * mm, "end": v(58.89, 18) * mm, "construction": true});
            skLineSegment(sketch, "E424", {"start": v(59.47, 17) * mm, "end": v(65.24, 17) * mm});
            skLineSegment(sketch, "E425", {"start": v(65.24, 17) * mm, "end": v(68.13, 12) * mm});
            skLineSegment(sketch, "E426", {"start": v(68.13, 12) * mm, "end": v(65.24, 7) * mm});
            skLineSegment(sketch, "E427", {"start": v(65.24, 7) * mm, "end": v(59.47, 7) * mm});
            skLineSegment(sketch, "E428", {"start": v(59.47, 7) * mm, "end": v(56.58, 12) * mm});
            skLineSegment(sketch, "E429", {"start": v(56.58, 12) * mm, "end": v(59.47, 17) * mm});
            skLineSegment(sketch, "E430", {"start": v(65.82, 18) * mm, "end": v(58.89, 18) * mm, "construction": true});
            skLineSegment(sketch, "E431", {"start": v(65.82, 6) * mm, "end": v(69.28, 12) * mm});
            skLineSegment(sketch, "E432", {"start": v(65.82, 30) * mm, "end": v(69.28, 24) * mm});
            skLineSegment(sketch, "E433", {"start": v(58.89, 18) * mm, "end": v(55.43, 24) * mm, "construction": true});
            skLineSegment(sketch, "E434", {"start": v(59.47, 29) * mm, "end": v(65.24, 29) * mm});
            skLineSegment(sketch, "E435", {"start": v(65.24, 29) * mm, "end": v(68.13, 24) * mm});
            skLineSegment(sketch, "E436", {"start": v(68.13, 24) * mm, "end": v(65.24, 19) * mm});
            skLineSegment(sketch, "E437", {"start": v(65.24, 19) * mm, "end": v(59.47, 19) * mm});
            skLineSegment(sketch, "E438", {"start": v(59.47, 19) * mm, "end": v(56.58, 24) * mm});
            skLineSegment(sketch, "E439", {"start": v(56.58, 24) * mm, "end": v(59.47, 29) * mm});
            skLineSegment(sketch, "E440", {"start": v(65.82, 30) * mm, "end": v(58.89, 30) * mm});
            skLineSegment(sketch, "E441", {"start": v(58.89, 30) * mm, "end": v(55.43, 36) * mm});
            skLineSegment(sketch, "E442", {"start": v(65.82, -30) * mm, "end": v(58.89, -30) * mm});
            skLineSegment(sketch, "E443", {"start": v(65.82, -18) * mm, "end": v(69.28, -24) * mm});
            skLineSegment(sketch, "E444", {"start": v(58.89, -30) * mm, "end": v(55.43, -24) * mm, "construction": true});
            skLineSegment(sketch, "E445", {"start": v(55.43, -24) * mm, "end": v(58.89, -18) * mm, "construction": true});
            skLineSegment(sketch, "E446", {"start": v(59.47, -19) * mm, "end": v(65.24, -19) * mm});
            skLineSegment(sketch, "E447", {"start": v(65.24, -19) * mm, "end": v(68.13, -24) * mm});
            skLineSegment(sketch, "E448", {"start": v(68.13, -24) * mm, "end": v(65.24, -29) * mm});
            skLineSegment(sketch, "E449", {"start": v(65.24, -29) * mm, "end": v(59.47, -29) * mm});
            skLineSegment(sketch, "E450", {"start": v(59.47, -29) * mm, "end": v(56.58, -24) * mm});
            skLineSegment(sketch, "E451", {"start": v(56.58, -24) * mm, "end": v(59.47, -19) * mm});
            skLineSegment(sketch, "E452", {"start": v(65.82, -18) * mm, "end": v(58.89, -18) * mm, "construction": true});
            skLineSegment(sketch, "E453", {"start": v(59.47, -7) * mm, "end": v(65.24, -7) * mm});
            skLineSegment(sketch, "E454", {"start": v(65.24, -7) * mm, "end": v(68.13, -12) * mm});
            skLineSegment(sketch, "E455", {"start": v(68.13, -12) * mm, "end": v(65.24, -17) * mm});
            skLineSegment(sketch, "E456", {"start": v(65.24, -17) * mm, "end": v(59.47, -17) * mm});
            skLineSegment(sketch, "E457", {"start": v(59.47, -17) * mm, "end": v(56.58, -12) * mm});
            skLineSegment(sketch, "E458", {"start": v(56.58, -12) * mm, "end": v(59.47, -7) * mm});
            skLineSegment(sketch, "E459", {"start": v(65.82, -18) * mm, "end": v(69.28, -12) * mm});
            skLineSegment(sketch, "E460", {"start": v(69.28, 0) * mm, "end": v(65.82, 6) * mm});
            skLineSegment(sketch, "E461", {"start": v(69.28, 12) * mm, "end": v(65.82, 18) * mm});
            skLineSegment(sketch, "E462", {"start": v(65.82, 18) * mm, "end": v(69.28, 24) * mm});
            skLineSegment(sketch, "E463", {"start": v(65.82, -30) * mm, "end": v(69.28, -24) * mm});
            skLineSegment(sketch, "E464", {"start": v(69.28, -12) * mm, "end": v(65.82, -6) * mm});
            skLineSegment(sketch, "E465", {"start": v(65.82, -6) * mm, "end": v(69.28, 0) * mm});
            skLineSegment(sketch, "E466", {"start": v(-69.28, 24) * mm, "end": v(-65.82, 30) * mm});
            skLineSegment(sketch, "E467", {"start": v(-69.28, -12) * mm, "end": v(-65.82, -18) * mm});
            skLineSegment(sketch, "E468", {"start": v(-69.28, -12) * mm, "end": v(-65.82, -6) * mm});
            skLineSegment(sketch, "E469", {"start": v(-65.82, -6) * mm, "end": v(-69.28, 0) * mm});
            skLineSegment(sketch, "E470", {"start": v(-69.28, 0) * mm, "end": v(-65.82, 6) * mm});
            skLineSegment(sketch, "E471", {"start": v(-65.24, 5) * mm, "end": v(-59.47, 5) * mm});
            skLineSegment(sketch, "E472", {"start": v(-59.47, 5) * mm, "end": v(-56.58, 0) * mm});
            skLineSegment(sketch, "E473", {"start": v(-56.58, 0) * mm, "end": v(-59.47, -5) * mm});
            skLineSegment(sketch, "E474", {"start": v(-59.47, -5) * mm, "end": v(-65.24, -5) * mm});
            skLineSegment(sketch, "E475", {"start": v(-65.24, -5) * mm, "end": v(-68.13, 0) * mm});
            skLineSegment(sketch, "E476", {"start": v(-68.13, 0) * mm, "end": v(-65.24, 5) * mm});
            skLineSegment(sketch, "E477", {"start": v(-58.89, 6) * mm, "end": v(-65.82, 6) * mm, "construction": true});
            skLineSegment(sketch, "E478", {"start": v(-65.82, -6) * mm, "end": v(-58.89, -6) * mm, "construction": true});
            skLineSegment(sketch, "E479", {"start": v(-65.82, 6) * mm, "end": v(-69.28, 12) * mm});
            skLineSegment(sketch, "E480", {"start": v(-69.28, 12) * mm, "end": v(-65.82, 18) * mm});
            skLineSegment(sketch, "E481", {"start": v(-65.24, 17) * mm, "end": v(-59.47, 17) * mm});
            skLineSegment(sketch, "E482", {"start": v(-59.47, 17) * mm, "end": v(-56.58, 12) * mm});
            skLineSegment(sketch, "E483", {"start": v(-56.58, 12) * mm, "end": v(-59.47, 7) * mm});
            skLineSegment(sketch, "E484", {"start": v(-59.47, 7) * mm, "end": v(-65.24, 7) * mm});
            skLineSegment(sketch, "E485", {"start": v(-65.24, 7) * mm, "end": v(-68.13, 12) * mm});
            skLineSegment(sketch, "E486", {"start": v(-68.13, 12) * mm, "end": v(-65.24, 17) * mm});
            skLineSegment(sketch, "E487", {"start": v(-58.89, 18) * mm, "end": v(-65.82, 18) * mm, "construction": true});
            skLineSegment(sketch, "E488", {"start": v(-58.89, 6) * mm, "end": v(-55.43, 12) * mm, "construction": true});
            skLineSegment(sketch, "E489", {"start": v(-58.89, 30) * mm, "end": v(-55.43, 24) * mm, "construction": true});
            skLineSegment(sketch, "E490", {"start": v(-65.82, 18) * mm, "end": v(-69.28, 24) * mm});
            skLineSegment(sketch, "E491", {"start": v(-65.24, 29) * mm, "end": v(-59.47, 29) * mm});
            skLineSegment(sketch, "E492", {"start": v(-59.47, 29) * mm, "end": v(-56.58, 24) * mm});
            skLineSegment(sketch, "E493", {"start": v(-56.58, 24) * mm, "end": v(-59.47, 19) * mm});
            skLineSegment(sketch, "E494", {"start": v(-59.47, 19) * mm, "end": v(-65.24, 19) * mm});
            skLineSegment(sketch, "E495", {"start": v(-65.24, 19) * mm, "end": v(-68.13, 24) * mm});
            skLineSegment(sketch, "E496", {"start": v(-68.13, 24) * mm, "end": v(-65.24, 29) * mm});
            skLineSegment(sketch, "E497", {"start": v(-58.89, 30) * mm, "end": v(-65.82, 30) * mm});
            skLineSegment(sketch, "E498", {"start": v(-58.89, 30) * mm, "end": v(-55.43, 36) * mm});
            skLineSegment(sketch, "E499", {"start": v(-58.89, -30) * mm, "end": v(-65.82, -30) * mm});
            skLineSegment(sketch, "E500", {"start": v(-58.89, -18) * mm, "end": v(-55.43, -24) * mm, "construction": true});
            skLineSegment(sketch, "E501", {"start": v(-65.82, -30) * mm, "end": v(-69.28, -24) * mm});
            skLineSegment(sketch, "E502", {"start": v(-69.28, -24) * mm, "end": v(-65.82, -18) * mm});
            skLineSegment(sketch, "E503", {"start": v(-65.24, -19) * mm, "end": v(-59.47, -19) * mm});
            skLineSegment(sketch, "E504", {"start": v(-59.47, -19) * mm, "end": v(-56.58, -24) * mm});
            skLineSegment(sketch, "E505", {"start": v(-56.58, -24) * mm, "end": v(-59.47, -29) * mm});
            skLineSegment(sketch, "E506", {"start": v(-59.47, -29) * mm, "end": v(-65.24, -29) * mm});
            skLineSegment(sketch, "E507", {"start": v(-65.24, -29) * mm, "end": v(-68.13, -24) * mm});
            skLineSegment(sketch, "E508", {"start": v(-68.13, -24) * mm, "end": v(-65.24, -19) * mm});
            skLineSegment(sketch, "E509", {"start": v(-58.89, -18) * mm, "end": v(-65.82, -18) * mm, "construction": true});
            skLineSegment(sketch, "E510", {"start": v(-65.24, -7) * mm, "end": v(-59.47, -7) * mm});
            skLineSegment(sketch, "E511", {"start": v(-59.47, -7) * mm, "end": v(-56.58, -12) * mm});
            skLineSegment(sketch, "E512", {"start": v(-56.58, -12) * mm, "end": v(-59.47, -17) * mm});
            skLineSegment(sketch, "E513", {"start": v(-59.47, -17) * mm, "end": v(-65.24, -17) * mm});
            skLineSegment(sketch, "E514", {"start": v(-65.24, -17) * mm, "end": v(-68.13, -12) * mm});
            skLineSegment(sketch, "E515", {"start": v(-68.13, -12) * mm, "end": v(-65.24, -7) * mm});
            skLineSegment(sketch, "E516", {"start": v(-58.89, -18) * mm, "end": v(-55.43, -12) * mm, "construction": true});
            skLineSegment(sketch, "E517", {"start": v(-48.5, 12) * mm, "end": v(-45.03, 6) * mm, "construction": true});
            skLineSegment(sketch, "E518", {"start": v(-55.43, 0) * mm, "end": v(-58.89, 6) * mm, "construction": true});
            skLineSegment(sketch, "E519", {"start": v(-54.85, 11) * mm, "end": v(-49.07, 11) * mm});
            skLineSegment(sketch, "E520", {"start": v(-49.07, 11) * mm, "end": v(-46.19, 6) * mm});
            skLineSegment(sketch, "E521", {"start": v(-46.19, 6) * mm, "end": v(-49.07, 1) * mm});
            skLineSegment(sketch, "E522", {"start": v(-49.07, 1) * mm, "end": v(-54.85, 1) * mm});
            skLineSegment(sketch, "E523", {"start": v(-54.85, 1) * mm, "end": v(-57.74, 6) * mm});
            skLineSegment(sketch, "E524", {"start": v(-57.74, 6) * mm, "end": v(-54.85, 11) * mm});
            skLineSegment(sketch, "E525", {"start": v(-48.5, 12) * mm, "end": v(-55.43, 12) * mm, "construction": true});
            skLineSegment(sketch, "E526", {"start": v(-55.43, 0) * mm, "end": v(-48.5, 0) * mm, "construction": true});
            skLineSegment(sketch, "E527", {"start": v(-48.5, 0) * mm, "end": v(-45.03, 6) * mm, "construction": true});
            skLineSegment(sketch, "E528", {"start": v(-48.5, 24) * mm, "end": v(-45.03, 18) * mm, "construction": true});
            skLineSegment(sketch, "E529", {"start": v(-55.43, 12) * mm, "end": v(-58.89, 18) * mm, "construction": true});
            skLineSegment(sketch, "E530", {"start": v(-58.89, 18) * mm, "end": v(-55.43, 24) * mm, "construction": true});
            skLineSegment(sketch, "E531", {"start": v(-54.85, 23) * mm, "end": v(-49.07, 23) * mm});
            skLineSegment(sketch, "E532", {"start": v(-49.07, 23) * mm, "end": v(-46.19, 18) * mm});
            skLineSegment(sketch, "E533", {"start": v(-46.19, 18) * mm, "end": v(-49.07, 13) * mm});
            skLineSegment(sketch, "E534", {"start": v(-49.07, 13) * mm, "end": v(-54.85, 13) * mm});
            skLineSegment(sketch, "E535", {"start": v(-54.85, 13) * mm, "end": v(-57.74, 18) * mm});
            skLineSegment(sketch, "E536", {"start": v(-57.74, 18) * mm, "end": v(-54.85, 23) * mm});
            skLineSegment(sketch, "E537", {"start": v(-48.5, 24) * mm, "end": v(-55.43, 24) * mm, "construction": true});
            skLineSegment(sketch, "E538", {"start": v(-48.5, 12) * mm, "end": v(-45.03, 18) * mm, "construction": true});
            skLineSegment(sketch, "E539", {"start": v(-48.5, 36) * mm, "end": v(-45.03, 30) * mm, "construction": true});
            skLineSegment(sketch, "E540", {"start": v(-54.85, 35) * mm, "end": v(-49.07, 35) * mm});
            skLineSegment(sketch, "E541", {"start": v(-49.07, 35) * mm, "end": v(-46.19, 30) * mm});
            skLineSegment(sketch, "E542", {"start": v(-46.19, 30) * mm, "end": v(-49.07, 25) * mm});
            skLineSegment(sketch, "E543", {"start": v(-49.07, 25) * mm, "end": v(-54.85, 25) * mm});
            skLineSegment(sketch, "E544", {"start": v(-54.85, 25) * mm, "end": v(-57.74, 30) * mm});
            skLineSegment(sketch, "E545", {"start": v(-57.74, 30) * mm, "end": v(-54.85, 35) * mm});
            skLineSegment(sketch, "E546", {"start": v(-48.5, 36) * mm, "end": v(-55.43, 36) * mm});
            skLineSegment(sketch, "E547", {"start": v(-48.5, 24) * mm, "end": v(-45.03, 30) * mm, "construction": true});
            skLineSegment(sketch, "E548", {"start": v(-48.5, 36) * mm, "end": v(-45.03, 42) * mm, "construction": true});
            skLineSegment(sketch, "E549", {"start": v(-48.5, -36) * mm, "end": v(-45.03, -42) * mm});
            skLineSegment(sketch, "E550", {"start": v(-48.5, -36) * mm, "end": v(-55.43, -36) * mm});
            skLineSegment(sketch, "E551", {"start": v(-48.5, -24) * mm, "end": v(-45.03, -30) * mm, "construction": true});
            skLineSegment(sketch, "E552", {"start": v(-55.43, -36) * mm, "end": v(-58.89, -30) * mm});
            skLineSegment(sketch, "E553", {"start": v(-58.89, -30) * mm, "end": v(-55.43, -24) * mm, "construction": true});
            skLineSegment(sketch, "E554", {"start": v(-54.85, -25) * mm, "end": v(-49.07, -25) * mm});
            skLineSegment(sketch, "E555", {"start": v(-49.07, -25) * mm, "end": v(-46.19, -30) * mm});
            skLineSegment(sketch, "E556", {"start": v(-46.19, -30) * mm, "end": v(-49.07, -35) * mm});
            skLineSegment(sketch, "E557", {"start": v(-49.07, -35) * mm, "end": v(-54.85, -35) * mm});
            skLineSegment(sketch, "E558", {"start": v(-54.85, -35) * mm, "end": v(-57.74, -30) * mm});
            skLineSegment(sketch, "E559", {"start": v(-57.74, -30) * mm, "end": v(-54.85, -25) * mm});
            skLineSegment(sketch, "E560", {"start": v(-48.5, -24) * mm, "end": v(-55.43, -24) * mm, "construction": true});
            skLineSegment(sketch, "E561", {"start": v(-48.5, -36) * mm, "end": v(-45.03, -30) * mm, "construction": true});
            skLineSegment(sketch, "E562", {"start": v(-48.5, -12) * mm, "end": v(-45.03, -18) * mm, "construction": true});
            skLineSegment(sketch, "E563", {"start": v(-54.85, -13) * mm, "end": v(-49.07, -13) * mm});
            skLineSegment(sketch, "E564", {"start": v(-49.07, -13) * mm, "end": v(-46.19, -18) * mm});
            skLineSegment(sketch, "E565", {"start": v(-46.19, -18) * mm, "end": v(-49.07, -23) * mm});
            skLineSegment(sketch, "E566", {"start": v(-49.07, -23) * mm, "end": v(-54.85, -23) * mm});
            skLineSegment(sketch, "E567", {"start": v(-54.85, -23) * mm, "end": v(-57.74, -18) * mm});
            skLineSegment(sketch, "E568", {"start": v(-57.74, -18) * mm, "end": v(-54.85, -13) * mm});
            skLineSegment(sketch, "E569", {"start": v(-48.5, -12) * mm, "end": v(-55.43, -12) * mm, "construction": true});
            skLineSegment(sketch, "E570", {"start": v(-48.5, -24) * mm, "end": v(-45.03, -18) * mm, "construction": true});
            skLineSegment(sketch, "E571", {"start": v(-48.5, 0) * mm, "end": v(-45.03, -6) * mm, "construction": true});
            skLineSegment(sketch, "E572", {"start": v(-55.43, -12) * mm, "end": v(-58.89, -6) * mm, "construction": true});
            skLineSegment(sketch, "E573", {"start": v(-58.89, -6) * mm, "end": v(-55.43, 0) * mm, "construction": true});
            skLineSegment(sketch, "E574", {"start": v(-54.85, -1) * mm, "end": v(-49.07, -1) * mm});
            skLineSegment(sketch, "E575", {"start": v(-49.07, -1) * mm, "end": v(-46.19, -6) * mm});
            skLineSegment(sketch, "E576", {"start": v(-46.19, -6) * mm, "end": v(-49.07, -11) * mm});
            skLineSegment(sketch, "E577", {"start": v(-49.07, -11) * mm, "end": v(-54.85, -11) * mm});
            skLineSegment(sketch, "E578", {"start": v(-54.85, -11) * mm, "end": v(-57.74, -6) * mm});
            skLineSegment(sketch, "E579", {"start": v(-57.74, -6) * mm, "end": v(-54.85, -1) * mm});
            skLineSegment(sketch, "E580", {"start": v(-48.5, -12) * mm, "end": v(-45.03, -6) * mm, "construction": true});
            skLineSegment(sketch, "E581", {"start": v(-45.03, -6) * mm, "end": v(-48.5, 0) * mm, "construction": true});
            skLineSegment(sketch, "E582", {"start": v(-44.46, 5) * mm, "end": v(-38.68, 5) * mm});
            skLineSegment(sketch, "E583", {"start": v(-38.68, 5) * mm, "end": v(-35.8, 0) * mm});
            skLineSegment(sketch, "E584", {"start": v(-35.8, 0) * mm, "end": v(-38.68, -5) * mm});
            skLineSegment(sketch, "E585", {"start": v(-38.68, -5) * mm, "end": v(-44.46, -5) * mm});
            skLineSegment(sketch, "E586", {"start": v(-44.46, -5) * mm, "end": v(-47.34, 0) * mm});
            skLineSegment(sketch, "E587", {"start": v(-47.34, 0) * mm, "end": v(-44.46, 5) * mm});
            skLineSegment(sketch, "E588", {"start": v(-38.1, 6) * mm, "end": v(-45.03, 6) * mm, "construction": true});
            skLineSegment(sketch, "E589", {"start": v(-45.03, -6) * mm, "end": v(-38.1, -6) * mm, "construction": true});
            skLineSegment(sketch, "E590", {"start": v(-45.03, 6) * mm, "end": v(-48.5, 12) * mm, "construction": true});
            skLineSegment(sketch, "E591", {"start": v(-44.46, 17) * mm, "end": v(-38.68, 17) * mm});
            skLineSegment(sketch, "E592", {"start": v(-38.68, 17) * mm, "end": v(-35.8, 12) * mm});
            skLineSegment(sketch, "E593", {"start": v(-35.8, 12) * mm, "end": v(-38.68, 7) * mm});
            skLineSegment(sketch, "E594", {"start": v(-38.68, 7) * mm, "end": v(-44.46, 7) * mm});
            skLineSegment(sketch, "E595", {"start": v(-44.46, 7) * mm, "end": v(-47.34, 12) * mm});
            skLineSegment(sketch, "E596", {"start": v(-47.34, 12) * mm, "end": v(-44.46, 17) * mm});
            skLineSegment(sketch, "E597", {"start": v(-38.1, 18) * mm, "end": v(-45.03, 18) * mm, "construction": true});
            skLineSegment(sketch, "E598", {"start": v(-38.1, 6) * mm, "end": v(-34.64, 12) * mm, "construction": true});
            skLineSegment(sketch, "E599", {"start": v(-38.1, 30) * mm, "end": v(-34.64, 24) * mm, "construction": true});
            skLineSegment(sketch, "E600", {"start": v(-45.03, 18) * mm, "end": v(-48.5, 24) * mm, "construction": true});
            skLineSegment(sketch, "E601", {"start": v(-44.46, 29) * mm, "end": v(-38.68, 29) * mm});
            skLineSegment(sketch, "E602", {"start": v(-38.68, 29) * mm, "end": v(-35.8, 24) * mm});
            skLineSegment(sketch, "E603", {"start": v(-35.8, 24) * mm, "end": v(-38.68, 19) * mm});
            skLineSegment(sketch, "E604", {"start": v(-38.68, 19) * mm, "end": v(-44.46, 19) * mm});
            skLineSegment(sketch, "E605", {"start": v(-44.46, 19) * mm, "end": v(-47.34, 24) * mm});
            skLineSegment(sketch, "E606", {"start": v(-47.34, 24) * mm, "end": v(-44.46, 29) * mm});
            skLineSegment(sketch, "E607", {"start": v(-38.1, 30) * mm, "end": v(-45.03, 30) * mm, "construction": true});
            skLineSegment(sketch, "E608", {"start": v(-45.03, 30) * mm, "end": v(-48.5, 36) * mm, "construction": true});
            skLineSegment(sketch, "E609", {"start": v(-48.5, 36) * mm, "end": v(-45.03, 42) * mm});
            skLineSegment(sketch, "E610", {"start": v(-44.46, 41) * mm, "end": v(-38.68, 41) * mm});
            skLineSegment(sketch, "E611", {"start": v(-38.68, 41) * mm, "end": v(-35.8, 36) * mm});
            skLineSegment(sketch, "E612", {"start": v(-35.8, 36) * mm, "end": v(-38.68, 31) * mm});
            skLineSegment(sketch, "E613", {"start": v(-38.68, 31) * mm, "end": v(-44.46, 31) * mm});
            skLineSegment(sketch, "E614", {"start": v(-44.46, 31) * mm, "end": v(-47.34, 36) * mm});
            skLineSegment(sketch, "E615", {"start": v(-47.34, 36) * mm, "end": v(-44.46, 41) * mm});
            skLineSegment(sketch, "E616", {"start": v(-38.1, 42) * mm, "end": v(-45.03, 42) * mm});
            skLineSegment(sketch, "E617", {"start": v(-38.1, 30) * mm, "end": v(-34.64, 36) * mm, "construction": true});
            skLineSegment(sketch, "E618", {"start": v(-38.1, -42) * mm, "end": v(-45.03, -42) * mm});
            skLineSegment(sketch, "E619", {"start": v(-45.03, -42) * mm, "end": v(-48.5, -36) * mm, "construction": true});
            skLineSegment(sketch, "E620", {"start": v(-44.46, -31) * mm, "end": v(-38.68, -31) * mm});
            skLineSegment(sketch, "E621", {"start": v(-38.68, -31) * mm, "end": v(-35.8, -36) * mm});
            skLineSegment(sketch, "E622", {"start": v(-35.8, -36) * mm, "end": v(-38.68, -41) * mm});
            skLineSegment(sketch, "E623", {"start": v(-38.68, -41) * mm, "end": v(-44.46, -41) * mm});
            skLineSegment(sketch, "E624", {"start": v(-44.46, -41) * mm, "end": v(-47.34, -36) * mm});
            skLineSegment(sketch, "E625", {"start": v(-47.34, -36) * mm, "end": v(-44.46, -31) * mm});
            skLineSegment(sketch, "E626", {"start": v(-38.1, -30) * mm, "end": v(-45.03, -30) * mm, "construction": true});
            skLineSegment(sketch, "E627", {"start": v(-38.1, -42) * mm, "end": v(-34.64, -36) * mm, "construction": true});
            skLineSegment(sketch, "E628", {"start": v(-38.1, -18) * mm, "end": v(-34.64, -24) * mm, "construction": true});
            skLineSegment(sketch, "E629", {"start": v(-45.03, -30) * mm, "end": v(-48.5, -24) * mm, "construction": true});
            skLineSegment(sketch, "E630", {"start": v(-44.46, -19) * mm, "end": v(-38.68, -19) * mm});
            skLineSegment(sketch, "E631", {"start": v(-38.68, -19) * mm, "end": v(-35.8, -24) * mm});
            skLineSegment(sketch, "E632", {"start": v(-35.8, -24) * mm, "end": v(-38.68, -29) * mm});
            skLineSegment(sketch, "E633", {"start": v(-38.68, -29) * mm, "end": v(-44.46, -29) * mm});
            skLineSegment(sketch, "E634", {"start": v(-44.46, -29) * mm, "end": v(-47.34, -24) * mm});
            skLineSegment(sketch, "E635", {"start": v(-47.34, -24) * mm, "end": v(-44.46, -19) * mm});
            skLineSegment(sketch, "E636", {"start": v(-38.1, -18) * mm, "end": v(-45.03, -18) * mm, "construction": true});
            skLineSegment(sketch, "E637", {"start": v(-45.03, -18) * mm, "end": v(-48.5, -12) * mm, "construction": true});
            skLineSegment(sketch, "E638", {"start": v(-44.46, -7) * mm, "end": v(-38.68, -7) * mm});
            skLineSegment(sketch, "E639", {"start": v(-38.68, -7) * mm, "end": v(-35.8, -12) * mm});
            skLineSegment(sketch, "E640", {"start": v(-35.8, -12) * mm, "end": v(-38.68, -17) * mm});
            skLineSegment(sketch, "E641", {"start": v(-38.68, -17) * mm, "end": v(-44.46, -17) * mm});
            skLineSegment(sketch, "E642", {"start": v(-44.46, -17) * mm, "end": v(-47.34, -12) * mm});
            skLineSegment(sketch, "E643", {"start": v(-47.34, -12) * mm, "end": v(-44.46, -7) * mm});
            skLineSegment(sketch, "E644", {"start": v(-38.1, -18) * mm, "end": v(-34.64, -12) * mm, "construction": true});
            skLineSegment(sketch, "E645", {"start": v(-34.64, 0) * mm, "end": v(-38.1, 6) * mm, "construction": true});
            skLineSegment(sketch, "E646", {"start": v(-34.06, 11) * mm, "end": v(-28.3, 11) * mm});
            skLineSegment(sketch, "E647", {"start": v(-28.3, 11) * mm, "end": v(-25.4, 6) * mm});
            skLineSegment(sketch, "E648", {"start": v(-25.4, 6) * mm, "end": v(-28.3, 1) * mm});
            skLineSegment(sketch, "E649", {"start": v(-28.3, 1) * mm, "end": v(-34.06, 1) * mm});
            skLineSegment(sketch, "E650", {"start": v(-34.06, 1) * mm, "end": v(-36.95, 6) * mm});
            skLineSegment(sketch, "E651", {"start": v(-36.95, 6) * mm, "end": v(-34.06, 11) * mm});
            skLineSegment(sketch, "E652", {"start": v(-27.71, 12) * mm, "end": v(-34.64, 12) * mm, "construction": true});
            skLineSegment(sketch, "E653", {"start": v(-34.64, 0) * mm, "end": v(-27.71, 0) * mm, "construction": true});
            skLineSegment(sketch, "E654", {"start": v(-34.64, 12) * mm, "end": v(-38.1, 18) * mm, "construction": true});
            skLineSegment(sketch, "E655", {"start": v(-38.1, 18) * mm, "end": v(-34.64, 24) * mm, "construction": true});
            skLineSegment(sketch, "E656", {"start": v(-34.06, 23) * mm, "end": v(-28.3, 23) * mm});
            skLineSegment(sketch, "E657", {"start": v(-28.3, 23) * mm, "end": v(-25.4, 18) * mm});
            skLineSegment(sketch, "E658", {"start": v(-25.4, 18) * mm, "end": v(-28.3, 13) * mm});
            skLineSegment(sketch, "E659", {"start": v(-28.3, 13) * mm, "end": v(-34.06, 13) * mm});
            skLineSegment(sketch, "E660", {"start": v(-34.06, 13) * mm, "end": v(-36.95, 18) * mm});
            skLineSegment(sketch, "E661", {"start": v(-36.95, 18) * mm, "end": v(-34.06, 23) * mm});
            skLineSegment(sketch, "E662", {"start": v(-27.71, 24) * mm, "end": v(-34.64, 24) * mm, "construction": true});
            skLineSegment(sketch, "E663", {"start": v(-34.06, 35) * mm, "end": v(-28.3, 35) * mm});
            skLineSegment(sketch, "E664", {"start": v(-28.3, 35) * mm, "end": v(-25.4, 30) * mm});
            skLineSegment(sketch, "E665", {"start": v(-25.4, 30) * mm, "end": v(-28.3, 25) * mm});
            skLineSegment(sketch, "E666", {"start": v(-28.3, 25) * mm, "end": v(-34.06, 25) * mm});
            skLineSegment(sketch, "E667", {"start": v(-34.06, 25) * mm, "end": v(-36.95, 30) * mm});
            skLineSegment(sketch, "E668", {"start": v(-36.95, 30) * mm, "end": v(-34.06, 35) * mm});
            skLineSegment(sketch, "E669", {"start": v(-27.71, 36) * mm, "end": v(-34.64, 36) * mm, "construction": true});
            skLineSegment(sketch, "E670", {"start": v(-27.71, 24) * mm, "end": v(-24.25, 30) * mm, "construction": true});
            skLineSegment(sketch, "E671", {"start": v(-27.71, 48) * mm, "end": v(-24.25, 42) * mm});
            skLineSegment(sketch, "E672", {"start": v(-34.64, 36) * mm, "end": v(-38.1, 42) * mm, "construction": true});
            skLineSegment(sketch, "E673", {"start": v(-38.1, 42) * mm, "end": v(-34.64, 48) * mm});
            skLineSegment(sketch, "E674", {"start": v(-34.06, 47) * mm, "end": v(-28.3, 47) * mm});
            skLineSegment(sketch, "E675", {"start": v(-28.3, 47) * mm, "end": v(-25.4, 42) * mm});
            skLineSegment(sketch, "E676", {"start": v(-25.4, 42) * mm, "end": v(-28.3, 37) * mm});
            skLineSegment(sketch, "E677", {"start": v(-28.3, 37) * mm, "end": v(-34.06, 37) * mm});
            skLineSegment(sketch, "E678", {"start": v(-34.06, 37) * mm, "end": v(-36.95, 42) * mm});
            skLineSegment(sketch, "E679", {"start": v(-36.95, 42) * mm, "end": v(-34.06, 47) * mm});
            skLineSegment(sketch, "E680", {"start": v(-27.71, 48) * mm, "end": v(-34.64, 48) * mm});
            skLineSegment(sketch, "E681", {"start": v(-34.64, -48) * mm, "end": v(-38.1, -42) * mm});
            skLineSegment(sketch, "E682", {"start": v(-34.06, -37) * mm, "end": v(-28.3, -37) * mm});
            skLineSegment(sketch, "E683", {"start": v(-28.3, -37) * mm, "end": v(-25.4, -42) * mm});
            skLineSegment(sketch, "E684", {"start": v(-25.4, -42) * mm, "end": v(-28.3, -47) * mm});
            skLineSegment(sketch, "E685", {"start": v(-28.3, -47) * mm, "end": v(-34.06, -47) * mm});
            skLineSegment(sketch, "E686", {"start": v(-34.06, -47) * mm, "end": v(-36.95, -42) * mm});
            skLineSegment(sketch, "E687", {"start": v(-36.95, -42) * mm, "end": v(-34.06, -37) * mm});
            skLineSegment(sketch, "E688", {"start": v(-27.71, -36) * mm, "end": v(-34.64, -36) * mm, "construction": true});
            skLineSegment(sketch, "E689", {"start": v(-34.64, -48) * mm, "end": v(-27.71, -48) * mm});
            skLineSegment(sketch, "E690", {"start": v(-27.71, -48) * mm, "end": v(-24.25, -42) * mm});
            skLineSegment(sketch, "E691", {"start": v(-34.64, -36) * mm, "end": v(-38.1, -30) * mm, "construction": true});
            skLineSegment(sketch, "E692", {"start": v(-38.1, -30) * mm, "end": v(-34.64, -24) * mm, "construction": true});
            skLineSegment(sketch, "E693", {"start": v(-34.06, -25) * mm, "end": v(-28.3, -25) * mm});
            skLineSegment(sketch, "E694", {"start": v(-28.3, -25) * mm, "end": v(-25.4, -30) * mm});
            skLineSegment(sketch, "E695", {"start": v(-25.4, -30) * mm, "end": v(-28.3, -35) * mm});
            skLineSegment(sketch, "E696", {"start": v(-28.3, -35) * mm, "end": v(-34.06, -35) * mm});
            skLineSegment(sketch, "E697", {"start": v(-34.06, -35) * mm, "end": v(-36.95, -30) * mm});
            skLineSegment(sketch, "E698", {"start": v(-36.95, -30) * mm, "end": v(-34.06, -25) * mm});
            skLineSegment(sketch, "E699", {"start": v(-27.71, -24) * mm, "end": v(-34.64, -24) * mm, "construction": true});
            skLineSegment(sketch, "E700", {"start": v(-27.71, -36) * mm, "end": v(-24.25, -30) * mm, "construction": true});
            skLineSegment(sketch, "E701", {"start": v(-27.71, -12) * mm, "end": v(-24.25, -18) * mm, "construction": true});
            skLineSegment(sketch, "E702", {"start": v(-34.06, -13) * mm, "end": v(-28.3, -13) * mm});
            skLineSegment(sketch, "E703", {"start": v(-28.3, -13) * mm, "end": v(-25.4, -18) * mm});
            skLineSegment(sketch, "E704", {"start": v(-25.4, -18) * mm, "end": v(-28.3, -23) * mm});
            skLineSegment(sketch, "E705", {"start": v(-28.3, -23) * mm, "end": v(-34.06, -23) * mm});
            skLineSegment(sketch, "E706", {"start": v(-34.06, -23) * mm, "end": v(-36.95, -18) * mm});
            skLineSegment(sketch, "E707", {"start": v(-36.95, -18) * mm, "end": v(-34.06, -13) * mm});
            skLineSegment(sketch, "E708", {"start": v(-27.71, -12) * mm, "end": v(-34.64, -12) * mm, "construction": true});
            skLineSegment(sketch, "E709", {"start": v(-34.64, -12) * mm, "end": v(-38.1, -6) * mm, "construction": true});
            skLineSegment(sketch, "E710", {"start": v(-38.1, -6) * mm, "end": v(-34.64, 0) * mm, "construction": true});
            skLineSegment(sketch, "E711", {"start": v(-34.06, -1) * mm, "end": v(-28.3, -1) * mm});
            skLineSegment(sketch, "E712", {"start": v(-28.3, -1) * mm, "end": v(-25.4, -6) * mm});
            skLineSegment(sketch, "E713", {"start": v(-25.4, -6) * mm, "end": v(-28.3, -11) * mm});
            skLineSegment(sketch, "E714", {"start": v(-28.3, -11) * mm, "end": v(-34.06, -11) * mm});
            skLineSegment(sketch, "E715", {"start": v(-34.06, -11) * mm, "end": v(-36.95, -6) * mm});
            skLineSegment(sketch, "E716", {"start": v(-36.95, -6) * mm, "end": v(-34.06, -1) * mm});
            skLineSegment(sketch, "E717", {"start": v(-27.71, -12) * mm, "end": v(-24.25, -6) * mm, "construction": true});
            skLineSegment(sketch, "E718", {"start": v(-24.25, -6) * mm, "end": v(-27.71, 0) * mm, "construction": true});
            skLineSegment(sketch, "E719", {"start": v(-27.71, 0) * mm, "end": v(-24.25, 6) * mm, "construction": true});
            skLineSegment(sketch, "E720", {"start": v(-23.67, 5) * mm, "end": v(-17.9, 5) * mm});
            skLineSegment(sketch, "E721", {"start": v(-17.9, 5) * mm, "end": v(-15.01, 0) * mm});
            skLineSegment(sketch, "E722", {"start": v(-15.01, 0) * mm, "end": v(-17.9, -5) * mm});
            skLineSegment(sketch, "E723", {"start": v(-17.9, -5) * mm, "end": v(-23.67, -5) * mm});
            skLineSegment(sketch, "E724", {"start": v(-23.67, -5) * mm, "end": v(-26.56, 0) * mm});
            skLineSegment(sketch, "E725", {"start": v(-26.56, 0) * mm, "end": v(-23.67, 5) * mm});
            skLineSegment(sketch, "E726", {"start": v(-17.32, 6) * mm, "end": v(-24.25, 6) * mm, "construction": true});
            skLineSegment(sketch, "E727", {"start": v(-24.25, -6) * mm, "end": v(-17.32, -6) * mm, "construction": true});
            skLineSegment(sketch, "E728", {"start": v(-24.25, 6) * mm, "end": v(-27.71, 12) * mm, "construction": true});
            skLineSegment(sketch, "E729", {"start": v(-27.71, 12) * mm, "end": v(-24.25, 18) * mm, "construction": true});
            skLineSegment(sketch, "E730", {"start": v(-23.67, 17) * mm, "end": v(-17.9, 17) * mm});
            skLineSegment(sketch, "E731", {"start": v(-17.9, 17) * mm, "end": v(-15.01, 12) * mm});
            skLineSegment(sketch, "E732", {"start": v(-15.01, 12) * mm, "end": v(-17.9, 7) * mm});
            skLineSegment(sketch, "E733", {"start": v(-17.9, 7) * mm, "end": v(-23.67, 7) * mm});
            skLineSegment(sketch, "E734", {"start": v(-23.67, 7) * mm, "end": v(-26.56, 12) * mm});
            skLineSegment(sketch, "E735", {"start": v(-26.56, 12) * mm, "end": v(-23.67, 17) * mm});
            skLineSegment(sketch, "E736", {"start": v(-17.32, 18) * mm, "end": v(-24.25, 18) * mm, "construction": true});
            skLineSegment(sketch, "E737", {"start": v(-17.32, 6) * mm, "end": v(-13.86, 12) * mm, "construction": true});
            skLineSegment(sketch, "E738", {"start": v(-17.32, 30) * mm, "end": v(-13.86, 24) * mm, "construction": true});
            skLineSegment(sketch, "E739", {"start": v(-24.25, 18) * mm, "end": v(-27.71, 24) * mm, "construction": true});
            skLineSegment(sketch, "E740", {"start": v(-23.67, 29) * mm, "end": v(-17.9, 29) * mm});
            skLineSegment(sketch, "E741", {"start": v(-17.9, 29) * mm, "end": v(-15.01, 24) * mm});
            skLineSegment(sketch, "E742", {"start": v(-15.01, 24) * mm, "end": v(-17.9, 19) * mm});
            skLineSegment(sketch, "E743", {"start": v(-17.9, 19) * mm, "end": v(-23.67, 19) * mm});
            skLineSegment(sketch, "E744", {"start": v(-23.67, 19) * mm, "end": v(-26.56, 24) * mm});
            skLineSegment(sketch, "E745", {"start": v(-26.56, 24) * mm, "end": v(-23.67, 29) * mm});
            skLineSegment(sketch, "E746", {"start": v(-17.32, 30) * mm, "end": v(-24.25, 30) * mm, "construction": true});
            skLineSegment(sketch, "E747", {"start": v(-24.25, 30) * mm, "end": v(-27.71, 36) * mm, "construction": true});
            skLineSegment(sketch, "E748", {"start": v(-27.71, 36) * mm, "end": v(-24.25, 42) * mm, "construction": true});
            skLineSegment(sketch, "E749", {"start": v(-23.67, 41) * mm, "end": v(-17.9, 41) * mm});
            skLineSegment(sketch, "E750", {"start": v(-17.9, 41) * mm, "end": v(-15.01, 36) * mm});
            skLineSegment(sketch, "E751", {"start": v(-15.01, 36) * mm, "end": v(-17.9, 31) * mm});
            skLineSegment(sketch, "E752", {"start": v(-17.9, 31) * mm, "end": v(-23.67, 31) * mm});
            skLineSegment(sketch, "E753", {"start": v(-23.67, 31) * mm, "end": v(-26.56, 36) * mm});
            skLineSegment(sketch, "E754", {"start": v(-26.56, 36) * mm, "end": v(-23.67, 41) * mm});
            skLineSegment(sketch, "E755", {"start": v(-17.32, 42) * mm, "end": v(-24.25, 42) * mm});
            skLineSegment(sketch, "E756", {"start": v(-17.32, 30) * mm, "end": v(-13.86, 36) * mm, "construction": true});
            skLineSegment(sketch, "E757", {"start": v(-17.32, -42) * mm, "end": v(-24.25, -42) * mm});
            skLineSegment(sketch, "E758", {"start": v(-24.25, -42) * mm, "end": v(-27.71, -36) * mm, "construction": true});
            skLineSegment(sketch, "E759", {"start": v(-23.67, -31) * mm, "end": v(-17.9, -31) * mm});
            skLineSegment(sketch, "E760", {"start": v(-17.9, -31) * mm, "end": v(-15.01, -36) * mm});
            skLineSegment(sketch, "E761", {"start": v(-15.01, -36) * mm, "end": v(-17.9, -41) * mm});
            skLineSegment(sketch, "E762", {"start": v(-17.9, -41) * mm, "end": v(-23.67, -41) * mm});
            skLineSegment(sketch, "E763", {"start": v(-23.67, -41) * mm, "end": v(-26.56, -36) * mm});
            skLineSegment(sketch, "E764", {"start": v(-26.56, -36) * mm, "end": v(-23.67, -31) * mm});
            skLineSegment(sketch, "E765", {"start": v(-17.32, -30) * mm, "end": v(-24.25, -30) * mm, "construction": true});
            skLineSegment(sketch, "E766", {"start": v(-17.32, -42) * mm, "end": v(-13.86, -36) * mm, "construction": true});
            skLineSegment(sketch, "E767", {"start": v(-17.32, -18) * mm, "end": v(-13.86, -24) * mm, "construction": true});
            skLineSegment(sketch, "E768", {"start": v(-24.25, -30) * mm, "end": v(-27.71, -24) * mm, "construction": true});
            skLineSegment(sketch, "E769", {"start": v(-27.71, -24) * mm, "end": v(-24.25, -18) * mm, "construction": true});
            skLineSegment(sketch, "E770", {"start": v(-23.67, -19) * mm, "end": v(-17.9, -19) * mm});
            skLineSegment(sketch, "E771", {"start": v(-17.9, -19) * mm, "end": v(-15.01, -24) * mm});
            skLineSegment(sketch, "E772", {"start": v(-15.01, -24) * mm, "end": v(-17.9, -29) * mm});
            skLineSegment(sketch, "E773", {"start": v(-17.9, -29) * mm, "end": v(-23.67, -29) * mm});
            skLineSegment(sketch, "E774", {"start": v(-23.67, -29) * mm, "end": v(-26.56, -24) * mm});
            skLineSegment(sketch, "E775", {"start": v(-26.56, -24) * mm, "end": v(-23.67, -19) * mm});
            skLineSegment(sketch, "E776", {"start": v(-17.32, -18) * mm, "end": v(-24.25, -18) * mm, "construction": true});
            skLineSegment(sketch, "E777", {"start": v(-23.67, -7) * mm, "end": v(-17.9, -7) * mm});
            skLineSegment(sketch, "E778", {"start": v(-17.9, -7) * mm, "end": v(-15.01, -12) * mm});
            skLineSegment(sketch, "E779", {"start": v(-15.01, -12) * mm, "end": v(-17.9, -17) * mm});
            skLineSegment(sketch, "E780", {"start": v(-17.9, -17) * mm, "end": v(-23.67, -17) * mm});
            skLineSegment(sketch, "E781", {"start": v(-23.67, -17) * mm, "end": v(-26.56, -12) * mm});
            skLineSegment(sketch, "E782", {"start": v(-26.56, -12) * mm, "end": v(-23.67, -7) * mm});
            skLineSegment(sketch, "E783", {"start": v(-17.32, -18) * mm, "end": v(-13.86, -12) * mm, "construction": true});
            skLineSegment(sketch, "E784", {"start": v(-6.93, 12) * mm, "end": v(-3.46, 6) * mm, "construction": true});
            skLineSegment(sketch, "E785", {"start": v(-13.86, 0) * mm, "end": v(-17.32, 6) * mm, "construction": true});
            skLineSegment(sketch, "E786", {"start": v(-13.28, 11) * mm, "end": v(-7.5, 11) * mm});
            skLineSegment(sketch, "E787", {"start": v(-7.5, 11) * mm, "end": v(-4.62, 6) * mm});
            skLineSegment(sketch, "E788", {"start": v(-4.62, 6) * mm, "end": v(-7.5, 1) * mm});
            skLineSegment(sketch, "E789", {"start": v(-7.5, 1) * mm, "end": v(-13.28, 1) * mm});
            skLineSegment(sketch, "E790", {"start": v(-13.28, 1) * mm, "end": v(-16.17, 6) * mm});
            skLineSegment(sketch, "E791", {"start": v(-16.17, 6) * mm, "end": v(-13.28, 11) * mm});
            skLineSegment(sketch, "E792", {"start": v(-6.93, 12) * mm, "end": v(-13.86, 12) * mm, "construction": true});
            skLineSegment(sketch, "E793", {"start": v(-13.86, 0) * mm, "end": v(-6.93, 0) * mm, "construction": true});
            skLineSegment(sketch, "E794", {"start": v(-6.93, 24) * mm, "end": v(-3.46, 18) * mm, "construction": true});
            skLineSegment(sketch, "E795", {"start": v(-13.86, 12) * mm, "end": v(-17.32, 18) * mm, "construction": true});
            skLineSegment(sketch, "E796", {"start": v(-17.32, 18) * mm, "end": v(-13.86, 24) * mm, "construction": true});
            skLineSegment(sketch, "E797", {"start": v(-13.28, 23) * mm, "end": v(-7.5, 23) * mm});
            skLineSegment(sketch, "E798", {"start": v(-7.5, 23) * mm, "end": v(-4.62, 18) * mm});
            skLineSegment(sketch, "E799", {"start": v(-4.62, 18) * mm, "end": v(-7.5, 13) * mm});
            skLineSegment(sketch, "E800", {"start": v(-7.5, 13) * mm, "end": v(-13.28, 13) * mm});
            skLineSegment(sketch, "E801", {"start": v(-13.28, 13) * mm, "end": v(-16.17, 18) * mm});
            skLineSegment(sketch, "E802", {"start": v(-16.17, 18) * mm, "end": v(-13.28, 23) * mm});
            skLineSegment(sketch, "E803", {"start": v(-6.93, 24) * mm, "end": v(-13.86, 24) * mm, "construction": true});
            skLineSegment(sketch, "E804", {"start": v(-6.93, 36) * mm, "end": v(-3.46, 30) * mm, "construction": true});
            skLineSegment(sketch, "E805", {"start": v(-13.28, 35) * mm, "end": v(-7.5, 35) * mm});
            skLineSegment(sketch, "E806", {"start": v(-7.5, 35) * mm, "end": v(-4.62, 30) * mm});
            skLineSegment(sketch, "E807", {"start": v(-4.62, 30) * mm, "end": v(-7.5, 25) * mm});
            skLineSegment(sketch, "E808", {"start": v(-7.5, 25) * mm, "end": v(-13.28, 25) * mm});
            skLineSegment(sketch, "E809", {"start": v(-13.28, 25) * mm, "end": v(-16.17, 30) * mm});
            skLineSegment(sketch, "E810", {"start": v(-16.17, 30) * mm, "end": v(-13.28, 35) * mm});
            skLineSegment(sketch, "E811", {"start": v(-6.93, 36) * mm, "end": v(-13.86, 36) * mm, "construction": true});
            skLineSegment(sketch, "E812", {"start": v(-6.93, 48) * mm, "end": v(-3.46, 42) * mm});
            skLineSegment(sketch, "E813", {"start": v(-13.86, 36) * mm, "end": v(-17.32, 42) * mm, "construction": true});
            skLineSegment(sketch, "E814", {"start": v(-17.32, 42) * mm, "end": v(-13.86, 48) * mm});
            skLineSegment(sketch, "E815", {"start": v(-13.28, 47) * mm, "end": v(-7.5, 47) * mm});
            skLineSegment(sketch, "E816", {"start": v(-7.5, 47) * mm, "end": v(-4.62, 42) * mm});
            skLineSegment(sketch, "E817", {"start": v(-4.62, 42) * mm, "end": v(-7.5, 37) * mm});
            skLineSegment(sketch, "E818", {"start": v(-7.5, 37) * mm, "end": v(-13.28, 37) * mm});
            skLineSegment(sketch, "E819", {"start": v(-13.28, 37) * mm, "end": v(-16.17, 42) * mm});
            skLineSegment(sketch, "E820", {"start": v(-16.17, 42) * mm, "end": v(-13.28, 47) * mm});
            skLineSegment(sketch, "E821", {"start": v(-6.93, 48) * mm, "end": v(-13.86, 48) * mm});
            skLineSegment(sketch, "E822", {"start": v(-6.93, -36) * mm, "end": v(-3.46, -42) * mm, "construction": true});
            skLineSegment(sketch, "E823", {"start": v(-13.86, -48) * mm, "end": v(-17.32, -42) * mm});
            skLineSegment(sketch, "E824", {"start": v(-13.28, -37) * mm, "end": v(-7.5, -37) * mm});
            skLineSegment(sketch, "E825", {"start": v(-7.5, -37) * mm, "end": v(-4.62, -42) * mm});
            skLineSegment(sketch, "E826", {"start": v(-4.62, -42) * mm, "end": v(-7.5, -47) * mm});
            skLineSegment(sketch, "E827", {"start": v(-7.5, -47) * mm, "end": v(-13.28, -47) * mm});
            skLineSegment(sketch, "E828", {"start": v(-13.28, -47) * mm, "end": v(-16.17, -42) * mm});
            skLineSegment(sketch, "E829", {"start": v(-16.17, -42) * mm, "end": v(-13.28, -37) * mm});
            skLineSegment(sketch, "E830", {"start": v(-6.93, -36) * mm, "end": v(-13.86, -36) * mm, "construction": true});
            skLineSegment(sketch, "E831", {"start": v(-13.86, -48) * mm, "end": v(-6.93, -48) * mm});
            skLineSegment(sketch, "E832", {"start": v(-6.93, -48) * mm, "end": v(-3.46, -42) * mm, "construction": true});
            skLineSegment(sketch, "E833", {"start": v(-6.93, -24) * mm, "end": v(-3.46, -30) * mm, "construction": true});
            skLineSegment(sketch, "E834", {"start": v(-13.86, -36) * mm, "end": v(-17.32, -30) * mm, "construction": true});
            skLineSegment(sketch, "E835", {"start": v(-17.32, -30) * mm, "end": v(-13.86, -24) * mm, "construction": true});
            skLineSegment(sketch, "E836", {"start": v(-13.28, -25) * mm, "end": v(-7.5, -25) * mm});
            skLineSegment(sketch, "E837", {"start": v(-7.5, -25) * mm, "end": v(-4.62, -30) * mm});
            skLineSegment(sketch, "E838", {"start": v(-4.62, -30) * mm, "end": v(-7.5, -35) * mm});
            skLineSegment(sketch, "E839", {"start": v(-7.5, -35) * mm, "end": v(-13.28, -35) * mm});
            skLineSegment(sketch, "E840", {"start": v(-13.28, -35) * mm, "end": v(-16.17, -30) * mm});
            skLineSegment(sketch, "E841", {"start": v(-16.17, -30) * mm, "end": v(-13.28, -25) * mm});
            skLineSegment(sketch, "E842", {"start": v(-6.93, -24) * mm, "end": v(-13.86, -24) * mm, "construction": true});
            skLineSegment(sketch, "E843", {"start": v(-6.93, -12) * mm, "end": v(-3.46, -18) * mm, "construction": true});
            skLineSegment(sketch, "E844", {"start": v(-13.28, -13) * mm, "end": v(-7.5, -13) * mm});
            skLineSegment(sketch, "E845", {"start": v(-7.5, -13) * mm, "end": v(-4.62, -18) * mm});
            skLineSegment(sketch, "E846", {"start": v(-4.62, -18) * mm, "end": v(-7.5, -23) * mm});
            skLineSegment(sketch, "E847", {"start": v(-7.5, -23) * mm, "end": v(-13.28, -23) * mm});
            skLineSegment(sketch, "E848", {"start": v(-13.28, -23) * mm, "end": v(-16.17, -18) * mm});
            skLineSegment(sketch, "E849", {"start": v(-16.17, -18) * mm, "end": v(-13.28, -13) * mm});
            skLineSegment(sketch, "E850", {"start": v(-6.93, -12) * mm, "end": v(-13.86, -12) * mm, "construction": true});
            skLineSegment(sketch, "E851", {"start": v(-6.93, 0) * mm, "end": v(-3.46, -6) * mm, "construction": true});
            skLineSegment(sketch, "E852", {"start": v(-13.86, -12) * mm, "end": v(-17.32, -6) * mm, "construction": true});
            skLineSegment(sketch, "E853", {"start": v(-17.32, -6) * mm, "end": v(-13.86, 0) * mm, "construction": true});
            skLineSegment(sketch, "E854", {"start": v(-13.28, -1) * mm, "end": v(-7.5, -1) * mm});
            skLineSegment(sketch, "E855", {"start": v(-7.5, -1) * mm, "end": v(-4.62, -6) * mm});
            skLineSegment(sketch, "E856", {"start": v(-4.62, -6) * mm, "end": v(-7.5, -11) * mm});
            skLineSegment(sketch, "E857", {"start": v(-7.5, -11) * mm, "end": v(-13.28, -11) * mm});
            skLineSegment(sketch, "E858", {"start": v(-13.28, -11) * mm, "end": v(-16.17, -6) * mm});
            skLineSegment(sketch, "E859", {"start": v(-16.17, -6) * mm, "end": v(-13.28, -1) * mm});
            skSolve(sketch);
        }
        {
            var Q0;
            Q0=makeQuery(id+"F0.imprint","IMPRINT",FACE,{"disambiguationData":[TD([[makeQuery(id+"F0.imprint","IMPRINT",EDGE,{"derivedFrom":sQuery(id+"F0.wireOp",EDGE,"E2")}),1.0]])]});
            extrude(context, id + "F1", {"entities" : qUnion([Q0]), "depth" : 20 * mm, "offsetDistance" : 25 * mm});
        }
        {
            var Q0;
            Q0=qCreatedBy(makeId("Top.planeOp"),FACE);
            cPlane(context, id + "F2", {"entities" : qUnion([Q0]), "cplaneType" : CPlaneType.OFFSET, "offset" : 20 * mm, "width" : 150 * mm, "height" : 150 * mm});
        }
        {
            var Q0;
            Q0=qCreatedBy(id+"F2.planeOp",FACE);
            var sketch = newSketch(context, id + "F3", { "sketchPlane" : qUnion([Q0])});
            skEllipse(sketch, "E860", {"center": v(0, 0) * mm, "majorRadius": 65 * mm, "minorRadius": 40 * mm, "majorAxis": v(1, 0)});
            skSolve(sketch);
        }
        {
            var Q0;
            Q0=qCreatedBy(makeId("Top.planeOp"),FACE);
            cPlane(context, id + "F4", {"entities" : qUnion([Q0]), "cplaneType" : CPlaneType.OFFSET, "offset" : 10 * mm, "width" : 150 * mm, "height" : 150 * mm});
        }
        {
            var Q0;
            Q0=qCreatedBy(id+"F4.planeOp",FACE);
            var sketch = newSketch(context, id + "F5", { "sketchPlane" : qUnion([Q0])});
            skEllipse(sketch, "E861", {"center": v(0, 0) * mm, "majorRadius": 40 * mm, "minorRadius": 22.5 * mm, "majorAxis": v(1, 0)});
            skSolve(sketch);
        }
        {
            var Q1;
            Q1=qSketchRegion(id+"F3",true);
            var Q2;
            Q2=qSketchRegion(id+"F5",true);
            loft(context, id + "F6", {"operationType" : NewBodyOperationType.REMOVE, "sheetProfilesArray" : [{ "sheetProfileEntities" : qUnion([Q1]) }, { "sheetProfileEntities" : qUnion([Q2]) }]});
        }
    });
